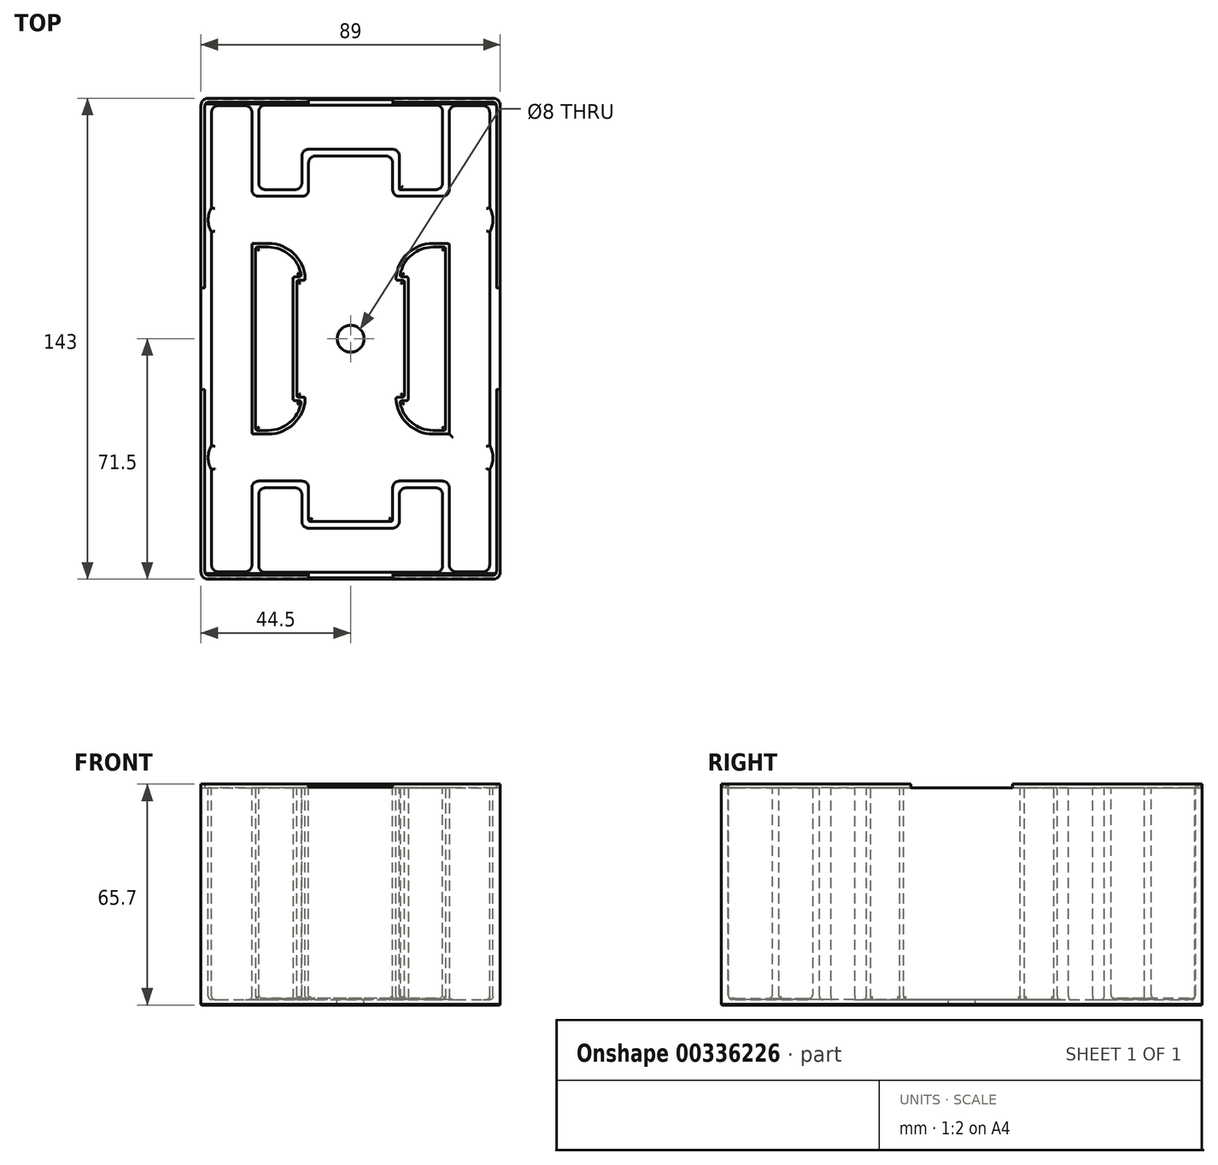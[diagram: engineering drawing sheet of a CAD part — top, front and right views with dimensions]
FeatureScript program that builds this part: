
annotation { "Feature Type Name" : "Feature", "Feature Type Description" : "" }
export const myFeature = defineFeature(function(context is Context, id is Id, definition is map)
    precondition{}
    {
        {
            var Q0;
            Q0=qCreatedBy(makeId("Top.planeOp"),FACE);
            var sketch = newSketch(context, id + "F0", { "sketchPlane" : qUnion([Q0])});
            skLineSegment(sketch, "E0.bottom", {"start": v(35.36, 35.36) * mm, "end": v(-35.36, 35.36) * mm, "construction": true});
            skLineSegment(sketch, "E0.top", {"start": v(35.36, -35.36) * mm, "end": v(-35.36, -35.36) * mm, "construction": true});
            skLineSegment(sketch, "E0.left", {"start": v(35.36, 35.36) * mm, "end": v(35.36, -35.36) * mm, "construction": true});
            skLineSegment(sketch, "E0.right", {"start": v(-35.36, 35.36) * mm, "end": v(-35.36, -35.36) * mm, "construction": true});
            skPoint(sketch, "E0.middle", {"position": v(0, 0) * mm});
            skLineSegment(sketch, "E1", {"start": v(35.36, 35.36) * mm, "end": v(-35.36, -35.36) * mm, "construction": true});
            skCircle(sketch, "E2", {"center": v(-35.36, 35.36) * mm, "radius": 34 * mm, "construction": true});
            skCircle(sketch, "E3.1.0", {"center": v(-35.36, -35.36) * mm, "radius": 34 * mm, "construction": true});
            skCircle(sketch, "E3.2.0", {"center": v(35.36, -35.36) * mm, "radius": 34 * mm, "construction": true});
            skCircle(sketch, "E3.3.0", {"center": v(35.36, 35.36) * mm, "radius": 34 * mm, "construction": true});
            skSolve(sketch);
        }
        {
            var Q0;
            Q0=qCreatedBy(makeId("Top.planeOp"),FACE);
            var sketch = newSketch(context, id + "F1", { "sketchPlane" : qUnion([Q0])});
            skLineSegment(sketch, "E4.0", {"start": v(35.36, 35.36) * mm, "end": v(-35.36, 35.36) * mm, "construction": true});
            skLineSegment(sketch, "E5.0", {"start": v(-35.36, 35.36) * mm, "end": v(-35.36, -35.36) * mm, "construction": true});
            skLineSegment(sketch, "E6.0", {"start": v(35.36, -35.36) * mm, "end": v(-35.36, -35.36) * mm, "construction": true});
            skLineSegment(sketch, "E7.0", {"start": v(35.36, 35.36) * mm, "end": v(35.36, -35.36) * mm, "construction": true});
            skArc(sketch, "E8", {"start": v(-35.36, 29.36) * mm, "mid": v(-41.36, 35.36) * mm, "end": v(-35.36, 41.36) * mm, "construction": true});
            skLineSegment(sketch, "E9", {"start": v(-35.36, 41.36) * mm, "end": v(0, 41.36) * mm, "construction": true});
            skLineSegment(sketch, "E10", {"start": v(-12.5, 0) * mm, "end": v(-12.5, 17.36) * mm, "construction": true});
            skLineSegment(sketch, "E11", {"start": v(-35.36, 29.36) * mm, "end": v(-24.5, 29.36) * mm, "construction": true});
            skPoint(sketch, "E12.visualSharp", {"position": v(-12.5, 29.36) * mm});
            skArc(sketch, "E12.filletArc", {"start": v(-12.5, 17.36) * mm, "mid": v(-16.01, 25.84) * mm, "end": v(-24.5, 29.36) * mm, "construction": true});
            skArc(sketch, "E13.MirrorCS", {"start": v(35.36, 29.36) * mm, "mid": v(41.36, 35.36) * mm, "end": v(35.36, 41.36) * mm, "construction": true});
            skLineSegment(sketch, "E14.MirrorCS", {"start": v(35.36, 41.36) * mm, "end": v(0, 41.36) * mm, "construction": true});
            skLineSegment(sketch, "E15.MirrorCS", {"start": v(35.36, 29.36) * mm, "end": v(24.5, 29.36) * mm, "construction": true});
            skArc(sketch, "E16.MirrorCS", {"start": v(12.5, 17.36) * mm, "mid": v(16.01, 25.84) * mm, "end": v(24.5, 29.36) * mm, "construction": true});
            skLineSegment(sketch, "E17.MirrorCS", {"start": v(12.5, 0) * mm, "end": v(12.5, 17.36) * mm, "construction": true});
            skArc(sketch, "E18.MirrorCS", {"start": v(-35.36, -29.36) * mm, "mid": v(-41.36, -35.36) * mm, "end": v(-35.36, -41.36) * mm, "construction": true});
            skArc(sketch, "E19.MirrorCS", {"start": v(35.36, -29.36) * mm, "mid": v(41.36, -35.36) * mm, "end": v(35.36, -41.36) * mm, "construction": true});
            skLineSegment(sketch, "E20.MirrorCS", {"start": v(35.36, -41.36) * mm, "end": v(0, -41.36) * mm, "construction": true});
            skLineSegment(sketch, "E21.MirrorCS", {"start": v(-35.36, -29.36) * mm, "end": v(-24.5, -29.36) * mm, "construction": true});
            skArc(sketch, "E22.MirrorCS", {"start": v(-12.5, -17.36) * mm, "mid": v(-16.01, -25.84) * mm, "end": v(-24.5, -29.36) * mm, "construction": true});
            skArc(sketch, "E23.MirrorCS", {"start": v(12.5, -17.36) * mm, "mid": v(16.01, -25.84) * mm, "end": v(24.5, -29.36) * mm, "construction": true});
            skLineSegment(sketch, "E24.MirrorCS", {"start": v(35.36, -29.36) * mm, "end": v(24.5, -29.36) * mm, "construction": true});
            skLineSegment(sketch, "E25.MirrorCS", {"start": v(-12.5, 0) * mm, "end": v(-12.5, -17.36) * mm, "construction": true});
            skLineSegment(sketch, "E26.MirrorCS", {"start": v(12.5, 0) * mm, "end": v(12.5, -17.36) * mm, "construction": true});
            skLineSegment(sketch, "E27.MirrorCS", {"start": v(-35.36, -41.36) * mm, "end": v(0, -41.36) * mm, "construction": true});
            skArc(sketch, "E28.0", {"start": v(-35.36, 28.36) * mm, "mid": v(-42.36, 35.36) * mm, "end": v(-35.36, 42.36) * mm});
            skLineSegment(sketch, "E28.1", {"start": v(-35.36, 28.36) * mm, "end": v(-24.5, 28.36) * mm});
            skArc(sketch, "E28.2", {"start": v(-13.5, 17.36) * mm, "mid": v(-16.72, 25.13) * mm, "end": v(-24.5, 28.36) * mm});
            skLineSegment(sketch, "E28.3", {"start": v(-13.5, 0) * mm, "end": v(-13.5, 17.36) * mm, "construction": true});
            skLineSegment(sketch, "E28.4", {"start": v(-13.5, 0) * mm, "end": v(-13.5, -17.36) * mm, "construction": true});
            skLineSegment(sketch, "E28.5", {"start": v(-35.36, 42.36) * mm, "end": v(0, 42.36) * mm});
            skArc(sketch, "E28.6", {"start": v(-13.5, -17.36) * mm, "mid": v(-16.72, -25.13) * mm, "end": v(-24.5, -28.36) * mm});
            skLineSegment(sketch, "E28.7", {"start": v(-35.36, -28.36) * mm, "end": v(-24.5, -28.36) * mm});
            skArc(sketch, "E28.8", {"start": v(-35.36, -28.36) * mm, "mid": v(-42.36, -35.36) * mm, "end": v(-35.36, -42.36) * mm});
            skLineSegment(sketch, "E28.9", {"start": v(-35.36, -42.36) * mm, "end": v(0, -42.36) * mm});
            skArc(sketch, "E28.10", {"start": v(13.5, 17.36) * mm, "mid": v(16.72, 25.13) * mm, "end": v(24.5, 28.36) * mm});
            skLineSegment(sketch, "E28.11", {"start": v(35.36, 28.36) * mm, "end": v(24.5, 28.36) * mm});
            skArc(sketch, "E28.12", {"start": v(35.36, 28.36) * mm, "mid": v(42.36, 35.36) * mm, "end": v(35.36, 42.36) * mm});
            skLineSegment(sketch, "E28.13", {"start": v(35.36, 42.36) * mm, "end": v(0, 42.36) * mm});
            skLineSegment(sketch, "E28.14", {"start": v(13.5, 0) * mm, "end": v(13.5, 17.36) * mm, "construction": true});
            skLineSegment(sketch, "E28.15", {"start": v(13.5, 0) * mm, "end": v(13.5, -17.36) * mm, "construction": true});
            skArc(sketch, "E28.16", {"start": v(13.5, -17.36) * mm, "mid": v(16.72, -25.13) * mm, "end": v(24.5, -28.36) * mm});
            skLineSegment(sketch, "E28.17", {"start": v(35.36, -28.36) * mm, "end": v(24.5, -28.36) * mm});
            skArc(sketch, "E28.18", {"start": v(35.36, -28.36) * mm, "mid": v(42.36, -35.36) * mm, "end": v(35.36, -42.36) * mm});
            skLineSegment(sketch, "E28.19", {"start": v(35.36, -42.36) * mm, "end": v(0, -42.36) * mm});
            skLineSegment(sketch, "E29", {"start": v(-13.5, 0) * mm, "end": v(-16, 0) * mm});
            skLineSegment(sketch, "E30", {"start": v(-16, 0) * mm, "end": v(-16, -17.36) * mm});
            skLineSegment(sketch, "E31", {"start": v(-16, -17.36) * mm, "end": v(-13.5, -17.36) * mm});
            skLineSegment(sketch, "E32.MirrorCS", {"start": v(13.5, 0) * mm, "end": v(16, 0) * mm});
            skLineSegment(sketch, "E33.MirrorCS", {"start": v(16, 0) * mm, "end": v(16, -17.36) * mm});
            skLineSegment(sketch, "E34.MirrorCS", {"start": v(16, -17.36) * mm, "end": v(13.5, -17.36) * mm});
            skLineSegment(sketch, "E35", {"start": v(-12.5, 42.36) * mm, "end": v(-12.5, 54.36) * mm});
            skLineSegment(sketch, "E36", {"start": v(-12.5, 54.36) * mm, "end": v(12.5, 54.36) * mm});
            skLineSegment(sketch, "E37", {"start": v(12.5, 54.36) * mm, "end": v(12.5, 42.36) * mm});
            skLineSegment(sketch, "E38", {"start": v(-13.5, 17.36) * mm, "end": v(-16, 17.36) * mm});
            skLineSegment(sketch, "E39", {"start": v(-16, 17.36) * mm, "end": v(-16, 0) * mm});
            skLineSegment(sketch, "E40", {"start": v(13.5, 17.36) * mm, "end": v(16, 17.36) * mm});
            skLineSegment(sketch, "E41", {"start": v(16, 17.36) * mm, "end": v(16, 0) * mm});
            skLineSegment(sketch, "E42.MirrorCS", {"start": v(-12.5, -42.36) * mm, "end": v(-12.5, -54.36) * mm});
            skLineSegment(sketch, "E43.MirrorCS", {"start": v(-12.5, -54.36) * mm, "end": v(12.5, -54.36) * mm});
            skLineSegment(sketch, "E44.MirrorCS", {"start": v(12.5, -54.36) * mm, "end": v(12.5, -42.36) * mm});
            skSolve(sketch);
        }
        {
            var Q0;
            Q0=qCreatedBy(makeId("Top.planeOp"),FACE);
            var sketch = newSketch(context, id + "F2", { "sketchPlane" : qUnion([Q0])});
            skCircle(sketch, "E45.0", {"center": v(-35.36, 35.36) * mm, "radius": 34 * mm, "construction": true});
            skCircle(sketch, "E46.0", {"center": v(35.36, 35.36) * mm, "radius": 34 * mm, "construction": true});
            skCircle(sketch, "E47.0", {"center": v(-35.36, -35.36) * mm, "radius": 34 * mm, "construction": true});
            skCircle(sketch, "E48.0", {"center": v(35.36, -35.36) * mm, "radius": 34 * mm, "construction": true});
            skLineSegment(sketch, "E49.0", {"start": v(35.36, -35.36) * mm, "end": v(-35.36, -35.36) * mm, "construction": true});
            skLineSegment(sketch, "E50.0", {"start": v(-35.36, 35.36) * mm, "end": v(-35.36, -35.36) * mm, "construction": true});
            skLineSegment(sketch, "E51.0", {"start": v(35.36, 35.36) * mm, "end": v(-35.36, 35.36) * mm, "construction": true});
            skLineSegment(sketch, "E52.0", {"start": v(35.36, 35.36) * mm, "end": v(35.36, -35.36) * mm, "construction": true});
            skLineSegment(sketch, "E53.bottom", {"start": v(-29.36, 69.36) * mm, "end": v(-41.36, 69.36) * mm});
            skLineSegment(sketch, "E53.top", {"start": v(-29.36, -69.36) * mm, "end": v(-41.36, -69.36) * mm});
            skLineSegment(sketch, "E53.left", {"start": v(-29.36, 69.36) * mm, "end": v(-29.36, -69.36) * mm});
            skLineSegment(sketch, "E53.right", {"start": v(-41.36, 69.36) * mm, "end": v(-41.36, -69.36) * mm});
            skPoint(sketch, "E53.middle", {"position": v(-35.36, 0) * mm});
            skLineSegment(sketch, "E54.bottom", {"start": v(41.36, 69.36) * mm, "end": v(29.36, 69.36) * mm});
            skLineSegment(sketch, "E54.top", {"start": v(41.36, -69.36) * mm, "end": v(29.36, -69.36) * mm});
            skLineSegment(sketch, "E54.left", {"start": v(41.36, 69.36) * mm, "end": v(41.36, -69.36) * mm});
            skLineSegment(sketch, "E54.right", {"start": v(29.36, 69.36) * mm, "end": v(29.36, -69.36) * mm});
            skPoint(sketch, "E54.middle", {"position": v(35.36, 0) * mm});
            skSolve(sketch);
        }
        {
            var Q0;
            Q0=qCreatedBy(makeId("Front.planeOp"),FACE);
            var sketch = newSketch(context, id + "F3", { "sketchPlane" : qUnion([Q0])});
            skLineSegment(sketch, "E55", {"start": v(0, 0) * mm, "end": v(0, -3) * mm});
            skLineSegment(sketch, "E56", {"start": v(0, -3) * mm, "end": v(0, -4.6) * mm});
            skLineSegment(sketch, "E57", {"start": v(0, 0) * mm, "end": v(0, 60) * mm});
            skLineSegment(sketch, "E58", {"start": v(0, 60) * mm, "end": v(0, 61.1) * mm});
            skSolve(sketch);
        }
        {
            var Q0;
            Q0=qCreatedBy(makeId("Top.planeOp"),FACE);
            var sketch = newSketch(context, id + "F4", { "sketchPlane" : qUnion([Q0])});
            skLineSegment(sketch, "E59.0.0", {"start": v(-41.36, -69.36) * mm, "end": v(-29.36, -69.36) * mm, "construction": true});
            skLineSegment(sketch, "E59.0.1", {"start": v(-29.36, -69.36) * mm, "end": v(-29.36, 69.36) * mm, "construction": true});
            skLineSegment(sketch, "E59.0.2", {"start": v(-29.36, 69.36) * mm, "end": v(-41.36, 69.36) * mm, "construction": true});
            skLineSegment(sketch, "E59.0.3", {"start": v(-41.36, 69.36) * mm, "end": v(-41.36, -69.36) * mm, "construction": true});
            skLineSegment(sketch, "E60.0.0", {"start": v(29.36, -69.36) * mm, "end": v(41.36, -69.36) * mm, "construction": true});
            skLineSegment(sketch, "E60.0.1", {"start": v(41.36, -69.36) * mm, "end": v(41.36, 69.36) * mm, "construction": true});
            skLineSegment(sketch, "E60.0.2", {"start": v(41.36, 69.36) * mm, "end": v(29.36, 69.36) * mm, "construction": true});
            skLineSegment(sketch, "E60.0.3", {"start": v(29.36, 69.36) * mm, "end": v(29.36, -69.36) * mm, "construction": true});
            skLineSegment(sketch, "E61.bottom", {"start": v(-44.5, 71.5) * mm, "end": v(44.5, 71.5) * mm});
            skLineSegment(sketch, "E61.top", {"start": v(-44.5, -71.5) * mm, "end": v(44.5, -71.5) * mm});
            skLineSegment(sketch, "E61.left", {"start": v(-44.5, 71.5) * mm, "end": v(-44.5, -71.5) * mm});
            skLineSegment(sketch, "E61.right", {"start": v(44.5, 71.5) * mm, "end": v(44.5, -71.5) * mm});
            skPoint(sketch, "E61.middle", {"position": v(0, 0) * mm});
            skPoint(sketch, "E62.0", {"position": v(42.36, -35.36) * mm});
            skSolve(sketch);
        }
        {
            var Q0;
            Q0 = qSketchRegion(id + "F4", true);
            var Q1;
            Q1=sQuery(id+"F3.wireOp",EDGE,"E57");
            var Q2;
            Q2=sQuery(id+"F3.wireOp",EDGE,"E58");
            sweep(context, id + "F5", {"profiles" : qUnion([Q0]), "path" : qUnion([Q1, Q2])});
        }
        {
            var Q0;
            Q0 = qSketchRegion(id + "F4", true);
            var Q1;
            Q1=sQuery(id+"F3.wireOp",EDGE,"E55");
            var Q2;
            Q2=sQuery(id+"F3.wireOp",EDGE,"E56");
            sweep(context, id + "F6", {"operationType" : NewBodyOperationType.ADD, "profiles" : qUnion([Q0]), "path" : qUnion([Q1, Q2])});
        }
        {
            var Q0;
            Q0 = qSketchRegion(id + "F1", true);
            var Q1;
            Q1=sQuery(id+"F3.wireOp",EDGE,"E57");
            var Q2;
            Q2=sQuery(id+"F3.wireOp",EDGE,"E58");
            sweep(context, id + "F7", {"operationType" : NewBodyOperationType.REMOVE, "profiles" : qUnion([Q0]), "path" : qUnion([Q1, Q2])});
        }
        {
            var Q0;
            Q0 = qSketchRegion(id + "F1", true);
            var Q1;
            Q1=sQuery(id+"F3.wireOp",EDGE,"E55");
            sweep(context, id + "F8", {"operationType" : NewBodyOperationType.REMOVE, "profiles" : qUnion([Q0]), "path" : qUnion([Q1])});
        }
        {
            var Q0;
            Q0 = qSketchRegion(id + "F2", true);
            var Q1;
            Q1=sQuery(id+"F3.wireOp",EDGE,"E57");
            var Q2;
            Q2=sQuery(id+"F3.wireOp",EDGE,"E58");
            sweep(context, id + "F9", {"operationType" : NewBodyOperationType.REMOVE, "profiles" : qUnion([Q0]), "path" : qUnion([Q1, Q2])});
        }
        {
            var Q0;
            Q0 = qSketchRegion(id + "F2", true);
            var Q1;
            Q1=sQuery(id+"F3.wireOp",EDGE,"E55");
            sweep(context, id + "F10", {"operationType" : NewBodyOperationType.REMOVE, "profiles" : qUnion([Q0]), "path" : qUnion([Q1])});
        }
        {
            var Q0;
            {var subQ5=sQuery(id+"F3.wireOp",EDGE,"E57");var subQ10=sQuery(id+"F4.wireOp",EDGE,"E61.right");var subQ11=sQuery(id+"F4.wireOp",EDGE,"E61.left");var subQ13=sQuery(id+"F4.wireOp",EDGE,"E61.top");var subQ15=sQuery(id+"F4.wireOp",EDGE,"E61.bottom");Q0=makeQuery(id+"F9.boolean.opBoolean","SPLIT",FACE,{"disambiguationData":[TD([makeQuery(id+"F5.opSweep","SWEPT_FACE",FACE,{"disambiguationData":[OSD([subQ5,subQ15])]})])],"derivedFrom":makeQuery(id+"F5.opSweep","CAP_FACE",FACE,{"disambiguationData":[OSD([sQuery(id+"F3.wireOp",VERTEX,"E58.end"),subQ15,subQ13,subQ11,subQ10])],"isStart":false})});}
            shell(context, id + "F11", {"entities" : qUnion([Q0]), "thickness" : 2 * mm});
        }
        {
            var Q0;
            {var subQ0=sQuery(id+"F3.wireOp",EDGE,"E57");var subQ5=sQuery(id+"F1.wireOp",EDGE,"E28.1");Q0=makeQuery(id+"F9.boolean.opBoolean","SPLIT",FACE,{"disambiguationData":[TD([makeQuery(id+"F7.boolean.opBoolean","COPY",FACE,{"derivedFrom":makeQuery(id+"F7.opSweep","SWEPT_FACE",FACE,{"disambiguationData":[OSD([subQ5,subQ0])]})})])],"derivedFrom":makeQuery(id+"F5.opSweep","CAP_FACE",FACE,{"disambiguationData":[OSD([sQuery(id+"F3.wireOp",VERTEX,"E58.end"),sQuery(id+"F4.wireOp",EDGE,"E61.bottom"),sQuery(id+"F4.wireOp",EDGE,"E61.top"),sQuery(id+"F4.wireOp",EDGE,"E61.left"),sQuery(id+"F4.wireOp",EDGE,"E61.right")])],"isStart":false})});}
            var sketch = newSketch(context, id + "F12", { "sketchPlane" : qUnion([Q0])});
            skLineSegment(sketch, "E63.0", {"start": v(-24.5, -27.26) * mm, "end": v(-28.26, -27.26) * mm});
            skArc(sketch, "E63.1", {"start": v(-14.66, -18.46) * mm, "mid": v(-17.9, -24.73) * mm, "end": v(-24.5, -27.26) * mm});
            skLineSegment(sketch, "E63.2", {"start": v(-28.26, -27.26) * mm, "end": v(-28.26, 27.26) * mm});
            skLineSegment(sketch, "E63.3", {"start": v(-17.1, -18.46) * mm, "end": v(-14.66, -18.46) * mm});
            skLineSegment(sketch, "E63.4", {"start": v(-28.26, 27.26) * mm, "end": v(-24.5, 27.26) * mm});
            skArc(sketch, "E63.5", {"start": v(-24.5, 27.26) * mm, "mid": v(-17.9, 24.73) * mm, "end": v(-14.66, 18.46) * mm});
            skLineSegment(sketch, "E63.6", {"start": v(-14.66, 18.46) * mm, "end": v(-17.1, 18.46) * mm});
            skLineSegment(sketch, "E63.7", {"start": v(-17.1, 18.46) * mm, "end": v(-17.1, -18.46) * mm});
            skLineSegment(sketch, "E64.MirrorCS", {"start": v(28.26, -27.26) * mm, "end": v(28.26, 27.26) * mm});
            skLineSegment(sketch, "E65.MirrorCS", {"start": v(28.26, 27.26) * mm, "end": v(24.5, 27.26) * mm});
            skArc(sketch, "E66.MirrorCS", {"start": v(24.5, 27.26) * mm, "mid": v(17.9, 24.73) * mm, "end": v(14.66, 18.46) * mm});
            skLineSegment(sketch, "E67.MirrorCS", {"start": v(14.66, 18.46) * mm, "end": v(17.1, 18.46) * mm});
            skLineSegment(sketch, "E68.MirrorCS", {"start": v(17.1, 18.46) * mm, "end": v(17.1, -18.46) * mm});
            skLineSegment(sketch, "E69.MirrorCS", {"start": v(17.1, -18.46) * mm, "end": v(14.66, -18.46) * mm});
            skArc(sketch, "E70.MirrorCS", {"start": v(14.66, -18.46) * mm, "mid": v(17.9, -24.73) * mm, "end": v(24.5, -27.26) * mm});
            skLineSegment(sketch, "E71.MirrorCS", {"start": v(24.5, -27.26) * mm, "end": v(28.26, -27.26) * mm});
            skSolve(sketch);
        }
        {
            var Q0;
            Q0 = qSketchRegion(id + "F12", true);
            var Q1;
            Q1=sQuery(id+"F3.wireOp",EDGE,"E58");
            var Q2;
            Q2=sQuery(id+"F3.wireOp",EDGE,"E57");
            var Q3;
            Q3=sQuery(id+"F3.wireOp",EDGE,"E55");
            sweep(context, id + "F13", {"operationType" : NewBodyOperationType.REMOVE, "profiles" : qUnion([Q0]), "path" : qUnion([Q1, Q2, Q3])});
        }
        {
            var Q0;
            {var subQ0=sQuery(id+"F2.wireOp",EDGE,"E53.right");var subQ1=sQuery(id+"F2.wireOp",EDGE,"E53.bottom");Q0=makeQuery(id+"F10.boolean.opBoolean","MERGE",EDGE,{"derivedFrom":[makeQuery(id+"F9.boolean.opBoolean","COPY",EDGE,{"derivedFrom":makeQuery(id+"F9.opSweep","SWEPT_EDGE",EDGE,{"disambiguationData":[OSD([subQ1,subQ0,sQuery(id+"F3.wireOp",EDGE,"E57")])]})}),makeQuery(id+"F10.opSweep","SWEPT_EDGE",EDGE,{"disambiguationData":[OSD([subQ1,subQ0,sQuery(id+"F3.wireOp",EDGE,"E55")])]})]});}
            var Q1;
            {var subQ0=sQuery(id+"F2.wireOp",EDGE,"E54.left");var subQ1=sQuery(id+"F2.wireOp",EDGE,"E54.bottom");Q1=makeQuery(id+"F10.boolean.opBoolean","MERGE",EDGE,{"derivedFrom":[makeQuery(id+"F9.boolean.opBoolean","COPY",EDGE,{"derivedFrom":makeQuery(id+"F9.opSweep","SWEPT_EDGE",EDGE,{"disambiguationData":[OSD([subQ1,subQ0,sQuery(id+"F3.wireOp",EDGE,"E57")])]})}),makeQuery(id+"F10.opSweep","SWEPT_EDGE",EDGE,{"disambiguationData":[OSD([subQ1,subQ0,sQuery(id+"F3.wireOp",EDGE,"E55")])]})]});}
            var Q2;
            {var subQ0=sQuery(id+"F2.wireOp",EDGE,"E53.right");var subQ1=sQuery(id+"F2.wireOp",EDGE,"E53.top");Q2=makeQuery(id+"F10.boolean.opBoolean","MERGE",EDGE,{"derivedFrom":[makeQuery(id+"F9.boolean.opBoolean","COPY",EDGE,{"derivedFrom":makeQuery(id+"F9.opSweep","SWEPT_EDGE",EDGE,{"disambiguationData":[OSD([subQ1,subQ0,sQuery(id+"F3.wireOp",EDGE,"E57")])]})}),makeQuery(id+"F10.opSweep","SWEPT_EDGE",EDGE,{"disambiguationData":[OSD([subQ1,subQ0,sQuery(id+"F3.wireOp",EDGE,"E55")])]})]});}
            var Q3;
            {var subQ0=sQuery(id+"F2.wireOp",EDGE,"E54.left");var subQ1=sQuery(id+"F2.wireOp",EDGE,"E54.top");Q3=makeQuery(id+"F10.boolean.opBoolean","MERGE",EDGE,{"derivedFrom":[makeQuery(id+"F9.boolean.opBoolean","COPY",EDGE,{"derivedFrom":makeQuery(id+"F9.opSweep","SWEPT_EDGE",EDGE,{"disambiguationData":[OSD([subQ1,subQ0,sQuery(id+"F3.wireOp",EDGE,"E57")])]})}),makeQuery(id+"F10.opSweep","SWEPT_EDGE",EDGE,{"disambiguationData":[OSD([subQ1,subQ0,sQuery(id+"F3.wireOp",EDGE,"E55")])]})]});}
            var Q4;
            {var subQ0=sQuery(id+"F2.wireOp",EDGE,"E53.left");var subQ1=sQuery(id+"F2.wireOp",EDGE,"E53.bottom");Q4=makeQuery(id+"F10.boolean.opBoolean","MERGE",EDGE,{"derivedFrom":[makeQuery(id+"F9.boolean.opBoolean","COPY",EDGE,{"derivedFrom":makeQuery(id+"F9.opSweep","SWEPT_EDGE",EDGE,{"disambiguationData":[OSD([subQ1,subQ0,sQuery(id+"F3.wireOp",EDGE,"E57")])]})}),makeQuery(id+"F10.opSweep","SWEPT_EDGE",EDGE,{"disambiguationData":[OSD([subQ1,subQ0,sQuery(id+"F3.wireOp",EDGE,"E55")])]})]});}
            var Q5;
            {var subQ0=sQuery(id+"F2.wireOp",EDGE,"E54.right");var subQ1=sQuery(id+"F2.wireOp",EDGE,"E54.bottom");Q5=makeQuery(id+"F10.boolean.opBoolean","MERGE",EDGE,{"derivedFrom":[makeQuery(id+"F9.boolean.opBoolean","COPY",EDGE,{"derivedFrom":makeQuery(id+"F9.opSweep","SWEPT_EDGE",EDGE,{"disambiguationData":[OSD([subQ1,subQ0,sQuery(id+"F3.wireOp",EDGE,"E57")])]})}),makeQuery(id+"F10.opSweep","SWEPT_EDGE",EDGE,{"disambiguationData":[OSD([subQ1,subQ0,sQuery(id+"F3.wireOp",EDGE,"E55")])]})]});}
            var Q6;
            {var subQ0=sQuery(id+"F2.wireOp",EDGE,"E53.left");var subQ1=sQuery(id+"F2.wireOp",EDGE,"E53.top");Q6=makeQuery(id+"F10.boolean.opBoolean","MERGE",EDGE,{"derivedFrom":[makeQuery(id+"F9.boolean.opBoolean","COPY",EDGE,{"derivedFrom":makeQuery(id+"F9.opSweep","SWEPT_EDGE",EDGE,{"disambiguationData":[OSD([subQ1,subQ0,sQuery(id+"F3.wireOp",EDGE,"E57")])]})}),makeQuery(id+"F10.opSweep","SWEPT_EDGE",EDGE,{"disambiguationData":[OSD([subQ1,subQ0,sQuery(id+"F3.wireOp",EDGE,"E55")])]})]});}
            var Q7;
            {var subQ0=sQuery(id+"F2.wireOp",EDGE,"E54.right");var subQ1=sQuery(id+"F2.wireOp",EDGE,"E54.top");Q7=makeQuery(id+"F10.boolean.opBoolean","MERGE",EDGE,{"derivedFrom":[makeQuery(id+"F9.boolean.opBoolean","COPY",EDGE,{"derivedFrom":makeQuery(id+"F9.opSweep","SWEPT_EDGE",EDGE,{"disambiguationData":[OSD([subQ1,subQ0,sQuery(id+"F3.wireOp",EDGE,"E57")])]})}),makeQuery(id+"F10.opSweep","SWEPT_EDGE",EDGE,{"disambiguationData":[OSD([subQ1,subQ0,sQuery(id+"F3.wireOp",EDGE,"E55")])]})]});}
            var Q8;
            {var subQ0=sQuery(id+"F4.wireOp",EDGE,"E61.right");var subQ1=sQuery(id+"F4.wireOp",EDGE,"E61.top");Q8=makeQuery(id+"F6.boolean.opBoolean","MERGE",EDGE,{"derivedFrom":[makeQuery(id+"F5.opSweep","SWEPT_EDGE",EDGE,{"disambiguationData":[OSD([sQuery(id+"F3.wireOp",EDGE,"E57"),subQ1,subQ0])]}),makeQuery(id+"F6.opSweep","SWEPT_EDGE",EDGE,{"disambiguationData":[OSD([sQuery(id+"F3.wireOp",EDGE,"E55"),subQ1,subQ0])]})]});}
            var Q9;
            {var subQ0=sQuery(id+"F4.wireOp",EDGE,"E61.left");var subQ1=sQuery(id+"F4.wireOp",EDGE,"E61.top");Q9=makeQuery(id+"F6.boolean.opBoolean","MERGE",EDGE,{"derivedFrom":[makeQuery(id+"F5.opSweep","SWEPT_EDGE",EDGE,{"disambiguationData":[OSD([sQuery(id+"F3.wireOp",EDGE,"E57"),subQ1,subQ0])]}),makeQuery(id+"F6.opSweep","SWEPT_EDGE",EDGE,{"disambiguationData":[OSD([sQuery(id+"F3.wireOp",EDGE,"E55"),subQ1,subQ0])]})]});}
            var Q10;
            {var subQ0=sQuery(id+"F4.wireOp",EDGE,"E61.right");var subQ1=sQuery(id+"F4.wireOp",EDGE,"E61.bottom");Q10=makeQuery(id+"F6.boolean.opBoolean","MERGE",EDGE,{"derivedFrom":[makeQuery(id+"F5.opSweep","SWEPT_EDGE",EDGE,{"disambiguationData":[OSD([sQuery(id+"F3.wireOp",EDGE,"E57"),subQ1,subQ0])]}),makeQuery(id+"F6.opSweep","SWEPT_EDGE",EDGE,{"disambiguationData":[OSD([sQuery(id+"F3.wireOp",EDGE,"E55"),subQ1,subQ0])]})]});}
            var Q11;
            {var subQ0=sQuery(id+"F4.wireOp",EDGE,"E61.left");var subQ1=sQuery(id+"F4.wireOp",EDGE,"E61.bottom");Q11=makeQuery(id+"F6.boolean.opBoolean","MERGE",EDGE,{"derivedFrom":[makeQuery(id+"F5.opSweep","SWEPT_EDGE",EDGE,{"disambiguationData":[OSD([sQuery(id+"F3.wireOp",EDGE,"E57"),subQ1,subQ0])]}),makeQuery(id+"F6.opSweep","SWEPT_EDGE",EDGE,{"disambiguationData":[OSD([sQuery(id+"F3.wireOp",EDGE,"E55"),subQ1,subQ0])]})]});}
            var Q12;
            {var subQ0=sQuery(id+"F3.wireOp",EDGE,"E55");var subQ1=sQuery(id+"F1.wireOp",EDGE,"E28.5");Q12=makeQuery(id+"F10.boolean.opBoolean","INTERSECT",EDGE,{"derivedFrom":[makeQuery(id+"F8.boolean.opBoolean","MERGE",FACE,{"derivedFrom":[makeQuery(id+"F7.boolean.opBoolean","COPY",FACE,{"derivedFrom":makeQuery(id+"F7.opSweep","SWEPT_FACE",FACE,{"disambiguationData":[OSD([subQ1,sQuery(id+"F3.wireOp",EDGE,"E57")])]})}),makeQuery(id+"F8.opSweep","SWEPT_FACE",FACE,{"disambiguationData":[OSD([subQ1,subQ0])]})]}),makeQuery(id+"F10.opSweep","SWEPT_FACE",FACE,{"disambiguationData":[OSD([sQuery(id+"F2.wireOp",EDGE,"E53.left"),subQ0])]})]});}
            var Q13;
            {var subQ0=sQuery(id+"F1.wireOp",EDGE,"E35");var subQ1=sQuery(id+"F1.wireOp",EDGE,"E28.5");Q13=makeQuery(id+"F8.boolean.opBoolean","MERGE",EDGE,{"derivedFrom":[makeQuery(id+"F7.boolean.opBoolean","COPY",EDGE,{"derivedFrom":makeQuery(id+"F7.opSweep","SWEPT_EDGE",EDGE,{"disambiguationData":[OSD([subQ1,subQ0,sQuery(id+"F3.wireOp",EDGE,"E57")])]})}),makeQuery(id+"F8.opSweep","SWEPT_EDGE",EDGE,{"disambiguationData":[OSD([subQ1,subQ0,sQuery(id+"F3.wireOp",EDGE,"E55")])]})]});}
            var Q14;
            {var subQ0=sQuery(id+"F1.wireOp",EDGE,"E37");var subQ1=sQuery(id+"F1.wireOp",EDGE,"E28.13");Q14=makeQuery(id+"F8.boolean.opBoolean","MERGE",EDGE,{"derivedFrom":[makeQuery(id+"F7.boolean.opBoolean","COPY",EDGE,{"derivedFrom":makeQuery(id+"F7.opSweep","SWEPT_EDGE",EDGE,{"disambiguationData":[OSD([subQ1,subQ0,sQuery(id+"F3.wireOp",EDGE,"E57")])]})}),makeQuery(id+"F8.opSweep","SWEPT_EDGE",EDGE,{"disambiguationData":[OSD([subQ1,subQ0,sQuery(id+"F3.wireOp",EDGE,"E55")])]})]});}
            var Q15;
            {var subQ0=sQuery(id+"F3.wireOp",EDGE,"E55");var subQ1=sQuery(id+"F1.wireOp",EDGE,"E28.13");Q15=makeQuery(id+"F10.boolean.opBoolean","INTERSECT",EDGE,{"derivedFrom":[makeQuery(id+"F8.boolean.opBoolean","MERGE",FACE,{"derivedFrom":[makeQuery(id+"F7.boolean.opBoolean","COPY",FACE,{"derivedFrom":makeQuery(id+"F7.opSweep","SWEPT_FACE",FACE,{"disambiguationData":[OSD([subQ1,sQuery(id+"F3.wireOp",EDGE,"E57")])]})}),makeQuery(id+"F8.opSweep","SWEPT_FACE",FACE,{"disambiguationData":[OSD([subQ1,subQ0])]})]}),makeQuery(id+"F10.opSweep","SWEPT_FACE",FACE,{"disambiguationData":[OSD([sQuery(id+"F2.wireOp",EDGE,"E54.right"),subQ0])]})]});}
            var Q16;
            {var subQ0=sQuery(id+"F1.wireOp",EDGE,"E36");var subQ1=sQuery(id+"F1.wireOp",EDGE,"E35");Q16=makeQuery(id+"F8.boolean.opBoolean","MERGE",EDGE,{"derivedFrom":[makeQuery(id+"F7.boolean.opBoolean","COPY",EDGE,{"derivedFrom":makeQuery(id+"F7.opSweep","SWEPT_EDGE",EDGE,{"disambiguationData":[OSD([subQ1,subQ0,sQuery(id+"F3.wireOp",EDGE,"E57")])]})}),makeQuery(id+"F8.opSweep","SWEPT_EDGE",EDGE,{"disambiguationData":[OSD([subQ1,subQ0,sQuery(id+"F3.wireOp",EDGE,"E55")])]})]});}
            var Q17;
            {var subQ0=sQuery(id+"F1.wireOp",EDGE,"E37");var subQ1=sQuery(id+"F1.wireOp",EDGE,"E36");Q17=makeQuery(id+"F8.boolean.opBoolean","MERGE",EDGE,{"derivedFrom":[makeQuery(id+"F7.boolean.opBoolean","COPY",EDGE,{"derivedFrom":makeQuery(id+"F7.opSweep","SWEPT_EDGE",EDGE,{"disambiguationData":[OSD([subQ1,subQ0,sQuery(id+"F3.wireOp",EDGE,"E57")])]})}),makeQuery(id+"F8.opSweep","SWEPT_EDGE",EDGE,{"disambiguationData":[OSD([subQ1,subQ0,sQuery(id+"F3.wireOp",EDGE,"E55")])]})]});}
            var Q18;
            Q18=makeQuery(id+"F11.opShell","OFFSET_EDGE",EDGE,{"disambiguationData":[OSD([sQuery(id+"F1.wireOp",EDGE,"E28.5"),sQuery(id+"F1.wireOp",EDGE,"E35"),sQuery(id+"F3.wireOp",EDGE,"E55"),sQuery(id+"F3.wireOp",EDGE,"E57")])]});
            var Q19;
            Q19=makeQuery(id+"F11.opShell","OFFSET_EDGE",EDGE,{"disambiguationData":[OSD([sQuery(id+"F1.wireOp",EDGE,"E28.5"),sQuery(id+"F2.wireOp",EDGE,"E53.left"),sQuery(id+"F3.wireOp",EDGE,"E55"),sQuery(id+"F3.wireOp",EDGE,"E57")])]});
            var Q20;
            Q20=makeQuery(id+"F11.opShell","OFFSET_EDGE",EDGE,{"disambiguationData":[OSD([sQuery(id+"F1.wireOp",EDGE,"E36"),sQuery(id+"F1.wireOp",EDGE,"E37"),sQuery(id+"F3.wireOp",EDGE,"E55"),sQuery(id+"F3.wireOp",EDGE,"E57")])]});
            var Q21;
            Q21=makeQuery(id+"F11.opShell","OFFSET_EDGE",EDGE,{"disambiguationData":[OSD([sQuery(id+"F1.wireOp",EDGE,"E35"),sQuery(id+"F1.wireOp",EDGE,"E36"),sQuery(id+"F3.wireOp",EDGE,"E55"),sQuery(id+"F3.wireOp",EDGE,"E57")])]});
            var Q22;
            {var subQ0=sQuery(id+"F3.wireOp",EDGE,"E55");var subQ1=sQuery(id+"F2.wireOp",EDGE,"E54.right");var subQ3=sQuery(id+"F1.wireOp",EDGE,"E28.13");var subQ4=sQuery(id+"F4.wireOp",EDGE,"E61.bottom");var subQ5=sQuery(id+"F3.wireOp",EDGE,"E57");Q22=makeQuery(id+"F11.opShell","TWEAK_EDGE",EDGE,{"derivedFrom":[makeQuery(id+"F6.boolean.opBoolean","MERGE",FACE,{"derivedFrom":[makeQuery(id+"F5.opSweep","SWEPT_FACE",FACE,{"disambiguationData":[OSD([subQ5,subQ4])]}),makeQuery(id+"F6.opSweep","SWEPT_FACE",FACE,{"disambiguationData":[OSD([subQ0,subQ4])]})]}),makeQuery(id+"F10.boolean.opBoolean","MERGE",FACE,{"derivedFrom":[makeQuery(id+"F9.boolean.opBoolean","COPY",FACE,{"disambiguationData":[TD([makeQuery(id+"F7.boolean.opBoolean","COPY",FACE,{"derivedFrom":makeQuery(id+"F7.opSweep","SWEPT_FACE",FACE,{"disambiguationData":[OSD([subQ3,subQ5])]})})])],"derivedFrom":makeQuery(id+"F9.opSweep","SWEPT_FACE",FACE,{"disambiguationData":[OSD([subQ1,subQ5])]})}),makeQuery(id+"F10.opSweep","SWEPT_FACE",FACE,{"disambiguationData":[OSD([subQ1,subQ0])]})]})]});}
            var Q23;
            Q23=makeQuery(id+"F11.opShell","OFFSET_EDGE",EDGE,{"disambiguationData":[OSD([sQuery(id+"F1.wireOp",EDGE,"E28.13"),sQuery(id+"F2.wireOp",EDGE,"E54.right"),sQuery(id+"F3.wireOp",EDGE,"E55"),sQuery(id+"F3.wireOp",EDGE,"E57")])]});
            var Q24;
            {var subQ0=sQuery(id+"F3.wireOp",EDGE,"E55");var subQ1=sQuery(id+"F2.wireOp",EDGE,"E53.left");var subQ2=sQuery(id+"F2.wireOp",EDGE,"E53.top");var subQ5=sQuery(id+"F3.wireOp",EDGE,"E57");var subQ6=sQuery(id+"F4.wireOp",EDGE,"E61.top");Q24=makeQuery(id+"F11.opShell","TWEAK_EDGE",EDGE,{"derivedFrom":[makeQuery(id+"F6.boolean.opBoolean","MERGE",FACE,{"derivedFrom":[makeQuery(id+"F5.opSweep","SWEPT_FACE",FACE,{"disambiguationData":[OSD([subQ5,subQ6])]}),makeQuery(id+"F6.opSweep","SWEPT_FACE",FACE,{"disambiguationData":[OSD([subQ0,subQ6])]})]}),makeQuery(id+"F10.boolean.opBoolean","MERGE",FACE,{"derivedFrom":[makeQuery(id+"F9.boolean.opBoolean","COPY",FACE,{"disambiguationData":[TD([makeQuery(id+"F9.opSweep","SWEPT_FACE",FACE,{"disambiguationData":[OSD([subQ2,subQ5])]})])],"derivedFrom":makeQuery(id+"F9.opSweep","SWEPT_FACE",FACE,{"disambiguationData":[OSD([subQ1,subQ5])]})}),makeQuery(id+"F10.opSweep","SWEPT_FACE",FACE,{"disambiguationData":[OSD([subQ1,subQ0])]})]})]});}
            var Q25;
            {var subQ0=sQuery(id+"F3.wireOp",EDGE,"E55");var subQ1=sQuery(id+"F2.wireOp",EDGE,"E54.right");var subQ4=sQuery(id+"F2.wireOp",EDGE,"E54.top");var subQ5=sQuery(id+"F4.wireOp",EDGE,"E61.top");var subQ6=sQuery(id+"F3.wireOp",EDGE,"E57");Q25=makeQuery(id+"F11.opShell","TWEAK_EDGE",EDGE,{"derivedFrom":[makeQuery(id+"F6.boolean.opBoolean","MERGE",FACE,{"derivedFrom":[makeQuery(id+"F5.opSweep","SWEPT_FACE",FACE,{"disambiguationData":[OSD([subQ6,subQ5])]}),makeQuery(id+"F6.opSweep","SWEPT_FACE",FACE,{"disambiguationData":[OSD([subQ0,subQ5])]})]}),makeQuery(id+"F10.boolean.opBoolean","MERGE",FACE,{"derivedFrom":[makeQuery(id+"F9.boolean.opBoolean","COPY",FACE,{"disambiguationData":[TD([makeQuery(id+"F9.opSweep","SWEPT_FACE",FACE,{"disambiguationData":[OSD([subQ4,subQ6])]})])],"derivedFrom":makeQuery(id+"F9.opSweep","SWEPT_FACE",FACE,{"disambiguationData":[OSD([subQ1,subQ6])]})}),makeQuery(id+"F10.opSweep","SWEPT_FACE",FACE,{"disambiguationData":[OSD([subQ1,subQ0])]})]})]});}
            var Q26;
            {var subQ0=sQuery(id+"F3.wireOp",EDGE,"E55");var subQ1=sQuery(id+"F1.wireOp",EDGE,"E28.19");var subQ2=sQuery(id+"F1.wireOp",EDGE,"E28.9");Q26=makeQuery(id+"F10.boolean.opBoolean","INTERSECT",EDGE,{"derivedFrom":[makeQuery(id+"F8.boolean.opBoolean","MERGE",FACE,{"derivedFrom":[makeQuery(id+"F7.boolean.opBoolean","COPY",FACE,{"derivedFrom":makeQuery(id+"F7.opSweep","SWEPT_FACE",FACE,{"disambiguationData":[OSD([subQ2,subQ1,sQuery(id+"F3.wireOp",EDGE,"E57")])]})}),makeQuery(id+"F8.opSweep","SWEPT_FACE",FACE,{"disambiguationData":[OSD([subQ2,subQ1,subQ0])]})]}),makeQuery(id+"F10.opSweep","SWEPT_FACE",FACE,{"disambiguationData":[OSD([sQuery(id+"F2.wireOp",EDGE,"E53.left"),subQ0])]})]});}
            var Q27;
            {var subQ0=sQuery(id+"F3.wireOp",EDGE,"E55");var subQ1=sQuery(id+"F1.wireOp",EDGE,"E28.19");var subQ2=sQuery(id+"F1.wireOp",EDGE,"E28.9");Q27=makeQuery(id+"F10.boolean.opBoolean","INTERSECT",EDGE,{"derivedFrom":[makeQuery(id+"F8.boolean.opBoolean","MERGE",FACE,{"derivedFrom":[makeQuery(id+"F7.boolean.opBoolean","COPY",FACE,{"derivedFrom":makeQuery(id+"F7.opSweep","SWEPT_FACE",FACE,{"disambiguationData":[OSD([subQ2,subQ1,sQuery(id+"F3.wireOp",EDGE,"E57")])]})}),makeQuery(id+"F8.opSweep","SWEPT_FACE",FACE,{"disambiguationData":[OSD([subQ2,subQ1,subQ0])]})]}),makeQuery(id+"F10.opSweep","SWEPT_FACE",FACE,{"disambiguationData":[OSD([sQuery(id+"F2.wireOp",EDGE,"E54.right"),subQ0])]})]});}
            var Q28;
            Q28=makeQuery(id+"F11.opShell","OFFSET_EDGE",EDGE,{"disambiguationData":[OSD([sQuery(id+"F1.wireOp",EDGE,"E28.9"),sQuery(id+"F1.wireOp",EDGE,"E28.19"),sQuery(id+"F2.wireOp",EDGE,"E53.left"),sQuery(id+"F3.wireOp",EDGE,"E55"),sQuery(id+"F3.wireOp",EDGE,"E57")])]});
            var Q29;
            Q29=makeQuery(id+"F11.opShell","OFFSET_EDGE",EDGE,{"disambiguationData":[OSD([sQuery(id+"F1.wireOp",EDGE,"E28.9"),sQuery(id+"F1.wireOp",EDGE,"E28.19"),sQuery(id+"F2.wireOp",EDGE,"E54.right"),sQuery(id+"F3.wireOp",EDGE,"E55"),sQuery(id+"F3.wireOp",EDGE,"E57")])]});
            var Q30;
            {var subQ0=sQuery(id+"F3.wireOp",EDGE,"E55");var subQ1=sQuery(id+"F2.wireOp",EDGE,"E53.left");var subQ3=sQuery(id+"F3.wireOp",EDGE,"E57");var subQ4=sQuery(id+"F1.wireOp",EDGE,"E28.5");var subQ5=sQuery(id+"F4.wireOp",EDGE,"E61.bottom");Q30=makeQuery(id+"F11.opShell","TWEAK_EDGE",EDGE,{"derivedFrom":[makeQuery(id+"F6.boolean.opBoolean","MERGE",FACE,{"derivedFrom":[makeQuery(id+"F5.opSweep","SWEPT_FACE",FACE,{"disambiguationData":[OSD([subQ3,subQ5])]}),makeQuery(id+"F6.opSweep","SWEPT_FACE",FACE,{"disambiguationData":[OSD([subQ0,subQ5])]})]}),makeQuery(id+"F10.boolean.opBoolean","MERGE",FACE,{"derivedFrom":[makeQuery(id+"F9.boolean.opBoolean","COPY",FACE,{"disambiguationData":[TD([makeQuery(id+"F7.boolean.opBoolean","COPY",FACE,{"derivedFrom":makeQuery(id+"F7.opSweep","SWEPT_FACE",FACE,{"disambiguationData":[OSD([subQ4,subQ3])]})})])],"derivedFrom":makeQuery(id+"F9.opSweep","SWEPT_FACE",FACE,{"disambiguationData":[OSD([subQ1,subQ3])]})}),makeQuery(id+"F10.opSweep","SWEPT_FACE",FACE,{"disambiguationData":[OSD([subQ1,subQ0])]})]})]});}
            var Q31;
            Q31=makeQuery(id+"F11.opShell","OFFSET_EDGE",EDGE,{"disambiguationData":[OSD([sQuery(id+"F1.wireOp",EDGE,"E42.MirrorCS"),sQuery(id+"F1.wireOp",EDGE,"E43.MirrorCS"),sQuery(id+"F3.wireOp",EDGE,"E55"),sQuery(id+"F3.wireOp",EDGE,"E57")])]});
            var Q32;
            Q32=makeQuery(id+"F11.opShell","OFFSET_EDGE",EDGE,{"disambiguationData":[OSD([sQuery(id+"F1.wireOp",EDGE,"E43.MirrorCS"),sQuery(id+"F1.wireOp",EDGE,"E44.MirrorCS"),sQuery(id+"F3.wireOp",EDGE,"E55"),sQuery(id+"F3.wireOp",EDGE,"E57")])]});
            var Q33;
            {var subQ0=sQuery(id+"F1.wireOp",EDGE,"E42.MirrorCS");var subQ1=sQuery(id+"F1.wireOp",EDGE,"E28.9");Q33=makeQuery(id+"F8.boolean.opBoolean","MERGE",EDGE,{"derivedFrom":[makeQuery(id+"F7.boolean.opBoolean","COPY",EDGE,{"derivedFrom":makeQuery(id+"F7.opSweep","SWEPT_EDGE",EDGE,{"disambiguationData":[OSD([subQ1,subQ0,sQuery(id+"F3.wireOp",EDGE,"E57")])]})}),makeQuery(id+"F8.opSweep","SWEPT_EDGE",EDGE,{"disambiguationData":[OSD([subQ1,subQ0,sQuery(id+"F3.wireOp",EDGE,"E55")])]})]});}
            var Q34;
            Q34=makeQuery(id+"F11.opShell","OFFSET_EDGE",EDGE,{"disambiguationData":[OSD([sQuery(id+"F1.wireOp",EDGE,"E28.19"),sQuery(id+"F1.wireOp",EDGE,"E44.MirrorCS"),sQuery(id+"F3.wireOp",EDGE,"E55"),sQuery(id+"F3.wireOp",EDGE,"E57")])]});
            var Q35;
            {var subQ0=sQuery(id+"F1.wireOp",EDGE,"E44.MirrorCS");var subQ1=sQuery(id+"F1.wireOp",EDGE,"E28.19");Q35=makeQuery(id+"F8.boolean.opBoolean","MERGE",EDGE,{"derivedFrom":[makeQuery(id+"F7.boolean.opBoolean","COPY",EDGE,{"derivedFrom":makeQuery(id+"F7.opSweep","SWEPT_EDGE",EDGE,{"disambiguationData":[OSD([subQ1,subQ0,sQuery(id+"F3.wireOp",EDGE,"E57")])]})}),makeQuery(id+"F8.opSweep","SWEPT_EDGE",EDGE,{"disambiguationData":[OSD([subQ1,subQ0,sQuery(id+"F3.wireOp",EDGE,"E55")])]})]});}
            var Q36;
            Q36=makeQuery(id+"F11.opShell","OFFSET_EDGE",EDGE,{"disambiguationData":[OSD([sQuery(id+"F1.wireOp",EDGE,"E28.9"),sQuery(id+"F1.wireOp",EDGE,"E42.MirrorCS"),sQuery(id+"F3.wireOp",EDGE,"E55"),sQuery(id+"F3.wireOp",EDGE,"E57")])]});
            fillet(context, id + "F14", {"entities" : qUnion([Q0, Q1, Q2, Q3, Q4, Q5, Q6, Q7, Q8, Q9, Q10, Q11, Q12, Q13, Q14, Q15, Q16, Q17, Q18, Q19, Q20, Q21, Q22, Q23, Q24, Q25, Q26, Q27, Q28, Q29, Q30, Q31, Q32, Q33, Q34, Q35, Q36]), "radius" : 2 * mm, "allowEdgeOverflow" : false});
        }
        {
            var Q0;
            {var subQ0=sQuery(id+"F3.wireOp",VERTEX,"E55.end");Q0=makeQuery(id+"F13.boolean.opBoolean","MERGE",FACE,{"derivedFrom":[makeQuery(id+"F10.boolean.opBoolean","MERGE",FACE,{"derivedFrom":[makeQuery(id+"F8.boolean.opBoolean","COPY",FACE,{"derivedFrom":makeQuery(id+"F8.opSweep","CAP_FACE",FACE,{"disambiguationData":[OSD([sQuery(id+"F1.wireOp",EDGE,"E28.0"),sQuery(id+"F1.wireOp",EDGE,"E28.1"),sQuery(id+"F1.wireOp",EDGE,"E28.2"),sQuery(id+"F1.wireOp",EDGE,"E28.3"),sQuery(id+"F1.wireOp",EDGE,"E28.5"),sQuery(id+"F1.wireOp",EDGE,"E28.6"),sQuery(id+"F1.wireOp",EDGE,"E28.7"),sQuery(id+"F1.wireOp",EDGE,"E28.8"),sQuery(id+"F1.wireOp",EDGE,"E28.9"),sQuery(id+"F1.wireOp",EDGE,"E28.10"),sQuery(id+"F1.wireOp",EDGE,"E28.11"),sQuery(id+"F1.wireOp",EDGE,"E28.12"),sQuery(id+"F1.wireOp",EDGE,"E28.13"),sQuery(id+"F1.wireOp",EDGE,"E28.14"),sQuery(id+"F1.wireOp",EDGE,"E28.16"),sQuery(id+"F1.wireOp",EDGE,"E28.17"),sQuery(id+"F1.wireOp",EDGE,"E28.18"),sQuery(id+"F1.wireOp",EDGE,"E28.19"),sQuery(id+"F1.wireOp",EDGE,"E29"),sQuery(id+"F1.wireOp",EDGE,"E30"),sQuery(id+"F1.wireOp",EDGE,"E31"),sQuery(id+"F1.wireOp",EDGE,"E32.MirrorCS"),sQuery(id+"F1.wireOp",EDGE,"E33.MirrorCS"),sQuery(id+"F1.wireOp",EDGE,"E34.MirrorCS"),sQuery(id+"F1.wireOp",EDGE,"E35"),sQuery(id+"F1.wireOp",EDGE,"E36"),sQuery(id+"F1.wireOp",EDGE,"E37"),subQ0])],"isStart":false})}),makeQuery(id+"F10.opSweep","CAP_FACE",FACE,{"disambiguationData":[OSD([sQuery(id+"F2.wireOp",EDGE,"E53.bottom"),sQuery(id+"F2.wireOp",EDGE,"E53.top"),sQuery(id+"F2.wireOp",EDGE,"E53.left"),sQuery(id+"F2.wireOp",EDGE,"E53.right"),subQ0])],"isStart":false}),makeQuery(id+"F10.opSweep","CAP_FACE",FACE,{"disambiguationData":[OSD([sQuery(id+"F2.wireOp",EDGE,"E54.bottom"),sQuery(id+"F2.wireOp",EDGE,"E54.top"),sQuery(id+"F2.wireOp",EDGE,"E54.left"),sQuery(id+"F2.wireOp",EDGE,"E54.right"),subQ0])],"isStart":false})]}),makeQuery(id+"F13.opSweep","CAP_FACE",FACE,{"disambiguationData":[OSD([subQ0,sQuery(id+"F12.wireOp",EDGE,"7293b043-83ef-4255-ae6d-b3dc5b9a2924.0"),sQuery(id+"F12.wireOp",EDGE,"7293b043-83ef-4255-ae6d-b3dc5b9a2924.1"),sQuery(id+"F12.wireOp",EDGE,"7293b043-83ef-4255-ae6d-b3dc5b9a2924.2"),sQuery(id+"F12.wireOp",EDGE,"7293b043-83ef-4255-ae6d-b3dc5b9a2924.3"),sQuery(id+"F12.wireOp",EDGE,"7293b043-83ef-4255-ae6d-b3dc5b9a2924.4"),sQuery(id+"F12.wireOp",EDGE,"7293b043-83ef-4255-ae6d-b3dc5b9a2924.5"),sQuery(id+"F12.wireOp",EDGE,"7293b043-83ef-4255-ae6d-b3dc5b9a2924.6"),sQuery(id+"F12.wireOp",EDGE,"7293b043-83ef-4255-ae6d-b3dc5b9a2924.7"),sQuery(id+"F12.wireOp",EDGE,"illqywf3-bTeU-BicJ-eL38-BuILVfbRQocb")])],"isStart":false}),makeQuery(id+"F13.opSweep","CAP_FACE",FACE,{"disambiguationData":[OSD([subQ0,sQuery(id+"F12.wireOp",EDGE,"70b18b86-a124-4c69-b360-074546a5286a0.MirrorCS"),sQuery(id+"F12.wireOp",EDGE,"e57e1a6b-d62b-49b2-a005-49e9c515f2e70.MirrorCS"),sQuery(id+"F12.wireOp",EDGE,"b5c8ba8e-675c-42c0-b8a6-c8ccde90b03b0.MirrorCS"),sQuery(id+"F12.wireOp",EDGE,"2b51d841-ab56-46fc-a233-bf4b134416720.MirrorCS"),sQuery(id+"F12.wireOp",EDGE,"2ce506aa-516a-486f-9163-cfcafb0629370.MirrorCS"),sQuery(id+"F12.wireOp",EDGE,"b170f0c0-2848-43ee-ab32-be4ed6cfa2f00.MirrorCS"),sQuery(id+"F12.wireOp",EDGE,"7071eb6a-4e67-4c53-ad75-c6296ee54e740.MirrorCS"),sQuery(id+"F12.wireOp",EDGE,"bdd4a403-c5b4-428f-abee-52623345626a0.MirrorCS"),sQuery(id+"F12.wireOp",EDGE,"96279677-90b9-4bf5-aae9-6bb9f1e2f9ed0.MirrorCS")])],"isStart":false})]});}
            var sketch = newSketch(context, id + "F15", { "sketchPlane" : qUnion([Q0])});
            skLineSegment(sketch, "E72.0", {"start": v(-29.36, 28.36) * mm, "end": v(-29.36, -28.36) * mm, "construction": true});
            skLineSegment(sketch, "E73.bottom", {"start": v(-29.36, 28.36) * mm, "end": v(-41.36, 28.36) * mm});
            skLineSegment(sketch, "E73.top", {"start": v(-29.36, 27.26) * mm, "end": v(-41.36, 27.26) * mm});
            skLineSegment(sketch, "E73.left", {"start": v(-29.36, 28.36) * mm, "end": v(-29.36, 27.26) * mm});
            skLineSegment(sketch, "E73.right", {"start": v(-41.36, 28.36) * mm, "end": v(-41.36, 27.26) * mm});
            skLineSegment(sketch, "E74.MirrorCS", {"start": v(-41.36, -28.36) * mm, "end": v(-41.36, -27.26) * mm});
            skLineSegment(sketch, "E75.MirrorCS", {"start": v(-29.36, -28.36) * mm, "end": v(-41.36, -28.36) * mm});
            skLineSegment(sketch, "E76.MirrorCS", {"start": v(-29.36, -27.26) * mm, "end": v(-41.36, -27.26) * mm});
            skLineSegment(sketch, "E77.MirrorCS", {"start": v(-29.36, -28.36) * mm, "end": v(-29.36, -27.26) * mm});
            skLineSegment(sketch, "E78.MirrorCS", {"start": v(29.36, 28.36) * mm, "end": v(41.36, 28.36) * mm});
            skLineSegment(sketch, "E79.MirrorCS", {"start": v(41.36, 28.36) * mm, "end": v(41.36, 27.26) * mm});
            skLineSegment(sketch, "E80.MirrorCS", {"start": v(29.36, 27.26) * mm, "end": v(41.36, 27.26) * mm});
            skLineSegment(sketch, "E81.MirrorCS", {"start": v(29.36, 28.36) * mm, "end": v(29.36, 27.26) * mm});
            skLineSegment(sketch, "E82.MirrorCS", {"start": v(29.36, -28.36) * mm, "end": v(29.36, -27.26) * mm});
            skLineSegment(sketch, "E83.MirrorCS", {"start": v(29.36, -27.26) * mm, "end": v(41.36, -27.26) * mm});
            skLineSegment(sketch, "E84.MirrorCS", {"start": v(29.36, -28.36) * mm, "end": v(41.36, -28.36) * mm});
            skLineSegment(sketch, "E85.MirrorCS", {"start": v(41.36, -28.36) * mm, "end": v(41.36, -27.26) * mm});
            skSolve(sketch);
        }
        {
            var Q0;
            Q0=makeQuery(id+"F13.boolean.opBoolean","COPY",EDGE,{"derivedFrom":makeQuery(id+"F13.opSweep","SWEPT_EDGE",EDGE,{"disambiguationData":[OSD([sQuery(id+"F3.wireOp",EDGE,"E58"),sQuery(id+"F12.wireOp",EDGE,"b170f0c0-2848-43ee-ab32-be4ed6cfa2f00.MirrorCS"),sQuery(id+"F12.wireOp",EDGE,"7071eb6a-4e67-4c53-ad75-c6296ee54e740.MirrorCS")])]})});
            var Q1;
            Q1=makeQuery(id+"F13.boolean.opBoolean","COPY",EDGE,{"derivedFrom":makeQuery(id+"F13.opSweep","SWEPT_EDGE",EDGE,{"disambiguationData":[OSD([sQuery(id+"F3.wireOp",EDGE,"E58"),sQuery(id+"F12.wireOp",EDGE,"2ce506aa-516a-486f-9163-cfcafb0629370.MirrorCS"),sQuery(id+"F12.wireOp",EDGE,"b170f0c0-2848-43ee-ab32-be4ed6cfa2f00.MirrorCS")])]})});
            var Q2;
            Q2=makeQuery(id+"F13.boolean.opBoolean","COPY",EDGE,{"derivedFrom":makeQuery(id+"F13.opSweep","SWEPT_EDGE",EDGE,{"disambiguationData":[OSD([sQuery(id+"F3.wireOp",EDGE,"E58"),sQuery(id+"F12.wireOp",EDGE,"7293b043-83ef-4255-ae6d-b3dc5b9a2924.3"),sQuery(id+"F12.wireOp",EDGE,"7293b043-83ef-4255-ae6d-b3dc5b9a2924.7")])]})});
            var Q3;
            Q3=makeQuery(id+"F13.boolean.opBoolean","COPY",EDGE,{"derivedFrom":makeQuery(id+"F13.opSweep","SWEPT_EDGE",EDGE,{"disambiguationData":[OSD([sQuery(id+"F3.wireOp",EDGE,"E58"),sQuery(id+"F12.wireOp",EDGE,"7293b043-83ef-4255-ae6d-b3dc5b9a2924.6"),sQuery(id+"F12.wireOp",EDGE,"7293b043-83ef-4255-ae6d-b3dc5b9a2924.7")])]})});
            var Q4;
            {var subQ0=sQuery(id+"F1.wireOp",EDGE,"E29");var subQ1=sQuery(id+"F1.wireOp",EDGE,"E28.4");var subQ2=sQuery(id+"F1.wireOp",EDGE,"E28.3");Q4=makeQuery(id+"F8.boolean.opBoolean","MERGE",EDGE,{"derivedFrom":[makeQuery(id+"F7.boolean.opBoolean","COPY",EDGE,{"derivedFrom":makeQuery(id+"F7.opSweep","SWEPT_EDGE",EDGE,{"disambiguationData":[OSD([subQ2,subQ1,subQ0,sQuery(id+"F3.wireOp",EDGE,"E57")])]})}),makeQuery(id+"F8.opSweep","SWEPT_EDGE",EDGE,{"disambiguationData":[OSD([subQ2,subQ1,subQ0,sQuery(id+"F3.wireOp",EDGE,"E55")])]})]});}
            var Q5;
            {var subQ0=sQuery(id+"F1.wireOp",EDGE,"E32.MirrorCS");var subQ1=sQuery(id+"F1.wireOp",EDGE,"E28.15");var subQ2=sQuery(id+"F1.wireOp",EDGE,"E28.14");Q5=makeQuery(id+"F8.boolean.opBoolean","MERGE",EDGE,{"derivedFrom":[makeQuery(id+"F7.boolean.opBoolean","COPY",EDGE,{"derivedFrom":makeQuery(id+"F7.opSweep","SWEPT_EDGE",EDGE,{"disambiguationData":[OSD([subQ2,subQ1,subQ0,sQuery(id+"F3.wireOp",EDGE,"E57")])]})}),makeQuery(id+"F8.opSweep","SWEPT_EDGE",EDGE,{"disambiguationData":[OSD([subQ2,subQ1,subQ0,sQuery(id+"F3.wireOp",EDGE,"E55")])]})]});}
            var Q6;
            {var subQ0=sQuery(id+"F1.wireOp",EDGE,"E34.MirrorCS");var subQ1=sQuery(id+"F1.wireOp",EDGE,"E28.16");var subQ2=sQuery(id+"F1.wireOp",EDGE,"E28.15");Q6=makeQuery(id+"F8.boolean.opBoolean","MERGE",EDGE,{"derivedFrom":[makeQuery(id+"F7.boolean.opBoolean","COPY",EDGE,{"derivedFrom":makeQuery(id+"F7.opSweep","SWEPT_EDGE",EDGE,{"disambiguationData":[OSD([subQ2,subQ1,subQ0,sQuery(id+"F3.wireOp",EDGE,"E57")])]})}),makeQuery(id+"F8.opSweep","SWEPT_EDGE",EDGE,{"disambiguationData":[OSD([subQ2,subQ1,subQ0,sQuery(id+"F3.wireOp",EDGE,"E55")])]})]});}
            var Q7;
            {var subQ0=sQuery(id+"F1.wireOp",EDGE,"E31");var subQ1=sQuery(id+"F1.wireOp",EDGE,"E28.6");var subQ2=sQuery(id+"F1.wireOp",EDGE,"E28.4");Q7=makeQuery(id+"F8.boolean.opBoolean","MERGE",EDGE,{"derivedFrom":[makeQuery(id+"F7.boolean.opBoolean","COPY",EDGE,{"derivedFrom":makeQuery(id+"F7.opSweep","SWEPT_EDGE",EDGE,{"disambiguationData":[OSD([subQ2,subQ1,subQ0,sQuery(id+"F3.wireOp",EDGE,"E57")])]})}),makeQuery(id+"F8.opSweep","SWEPT_EDGE",EDGE,{"disambiguationData":[OSD([subQ2,subQ1,subQ0,sQuery(id+"F3.wireOp",EDGE,"E55")])]})]});}
            var Q8;
            {var subQ0=sQuery(id+"F1.wireOp",EDGE,"E33.MirrorCS");var subQ1=sQuery(id+"F1.wireOp",EDGE,"E32.MirrorCS");Q8=makeQuery(id+"F8.boolean.opBoolean","MERGE",EDGE,{"derivedFrom":[makeQuery(id+"F7.boolean.opBoolean","COPY",EDGE,{"derivedFrom":makeQuery(id+"F7.opSweep","SWEPT_EDGE",EDGE,{"disambiguationData":[OSD([subQ1,subQ0,sQuery(id+"F3.wireOp",EDGE,"E57")])]})}),makeQuery(id+"F8.opSweep","SWEPT_EDGE",EDGE,{"disambiguationData":[OSD([subQ1,subQ0,sQuery(id+"F3.wireOp",EDGE,"E55")])]})]});}
            var Q9;
            {var subQ0=sQuery(id+"F1.wireOp",EDGE,"E34.MirrorCS");var subQ1=sQuery(id+"F1.wireOp",EDGE,"E33.MirrorCS");Q9=makeQuery(id+"F8.boolean.opBoolean","MERGE",EDGE,{"derivedFrom":[makeQuery(id+"F7.boolean.opBoolean","COPY",EDGE,{"derivedFrom":makeQuery(id+"F7.opSweep","SWEPT_EDGE",EDGE,{"disambiguationData":[OSD([subQ1,subQ0,sQuery(id+"F3.wireOp",EDGE,"E57")])]})}),makeQuery(id+"F8.opSweep","SWEPT_EDGE",EDGE,{"disambiguationData":[OSD([subQ1,subQ0,sQuery(id+"F3.wireOp",EDGE,"E55")])]})]});}
            var Q10;
            {var subQ0=sQuery(id+"F1.wireOp",EDGE,"E30");var subQ1=sQuery(id+"F1.wireOp",EDGE,"E29");Q10=makeQuery(id+"F8.boolean.opBoolean","MERGE",EDGE,{"derivedFrom":[makeQuery(id+"F7.boolean.opBoolean","COPY",EDGE,{"derivedFrom":makeQuery(id+"F7.opSweep","SWEPT_EDGE",EDGE,{"disambiguationData":[OSD([subQ1,subQ0,sQuery(id+"F3.wireOp",EDGE,"E57")])]})}),makeQuery(id+"F8.opSweep","SWEPT_EDGE",EDGE,{"disambiguationData":[OSD([subQ1,subQ0,sQuery(id+"F3.wireOp",EDGE,"E55")])]})]});}
            var Q11;
            {var subQ0=sQuery(id+"F1.wireOp",EDGE,"E31");var subQ1=sQuery(id+"F1.wireOp",EDGE,"E30");Q11=makeQuery(id+"F8.boolean.opBoolean","MERGE",EDGE,{"derivedFrom":[makeQuery(id+"F7.boolean.opBoolean","COPY",EDGE,{"derivedFrom":makeQuery(id+"F7.opSweep","SWEPT_EDGE",EDGE,{"disambiguationData":[OSD([subQ1,subQ0,sQuery(id+"F3.wireOp",EDGE,"E57")])]})}),makeQuery(id+"F8.opSweep","SWEPT_EDGE",EDGE,{"disambiguationData":[OSD([subQ1,subQ0,sQuery(id+"F3.wireOp",EDGE,"E55")])]})]});}
            var Q12;
            Q12=makeQuery(id+"F13.boolean.opBoolean","COPY",EDGE,{"derivedFrom":makeQuery(id+"F13.opSweep","SWEPT_EDGE",EDGE,{"disambiguationData":[OSD([sQuery(id+"F2.wireOp",EDGE,"E53.left"),sQuery(id+"F3.wireOp",VERTEX,"E58.end"),sQuery(id+"F3.wireOp",EDGE,"E58"),sQuery(id+"F12.wireOp",EDGE,"7293b043-83ef-4255-ae6d-b3dc5b9a2924.4"),sQuery(id+"F12.wireOp",EDGE,"illqywf3-bTeU-BicJ-eL38-BuILVfbRQocb")])]})});
            var Q13;
            {var subQ0=sQuery(id+"F3.wireOp",EDGE,"E55");var subQ1=sQuery(id+"F1.wireOp",EDGE,"E28.7");Q13=makeQuery(id+"F10.boolean.opBoolean","INTERSECT",EDGE,{"derivedFrom":[makeQuery(id+"F8.boolean.opBoolean","MERGE",FACE,{"derivedFrom":[makeQuery(id+"F7.boolean.opBoolean","COPY",FACE,{"derivedFrom":makeQuery(id+"F7.opSweep","SWEPT_FACE",FACE,{"disambiguationData":[OSD([subQ1,sQuery(id+"F3.wireOp",EDGE,"E57")])]})}),makeQuery(id+"F8.opSweep","SWEPT_FACE",FACE,{"disambiguationData":[OSD([subQ1,subQ0])]})]}),makeQuery(id+"F10.opSweep","SWEPT_FACE",FACE,{"disambiguationData":[OSD([sQuery(id+"F2.wireOp",EDGE,"E53.left"),subQ0])]})]});}
            var Q14;
            {var subQ0=sQuery(id+"F3.wireOp",EDGE,"E55");var subQ1=sQuery(id+"F1.wireOp",EDGE,"E28.1");Q14=makeQuery(id+"F10.boolean.opBoolean","INTERSECT",EDGE,{"derivedFrom":[makeQuery(id+"F8.boolean.opBoolean","MERGE",FACE,{"derivedFrom":[makeQuery(id+"F7.boolean.opBoolean","COPY",FACE,{"derivedFrom":makeQuery(id+"F7.opSweep","SWEPT_FACE",FACE,{"disambiguationData":[OSD([subQ1,sQuery(id+"F3.wireOp",EDGE,"E57")])]})}),makeQuery(id+"F8.opSweep","SWEPT_FACE",FACE,{"disambiguationData":[OSD([subQ1,subQ0])]})]}),makeQuery(id+"F10.opSweep","SWEPT_FACE",FACE,{"disambiguationData":[OSD([sQuery(id+"F2.wireOp",EDGE,"E53.left"),subQ0])]})]});}
            var Q15;
            Q15=makeQuery(id+"F13.boolean.opBoolean","COPY",EDGE,{"derivedFrom":makeQuery(id+"F13.opSweep","SWEPT_EDGE",EDGE,{"disambiguationData":[OSD([sQuery(id+"F2.wireOp",EDGE,"E53.left"),sQuery(id+"F3.wireOp",VERTEX,"E58.end"),sQuery(id+"F3.wireOp",EDGE,"E58"),sQuery(id+"F12.wireOp",EDGE,"7293b043-83ef-4255-ae6d-b3dc5b9a2924.0"),sQuery(id+"F12.wireOp",EDGE,"illqywf3-bTeU-BicJ-eL38-BuILVfbRQocb")])]})});
            var Q16;
            Q16=makeQuery(id+"F13.boolean.opBoolean","COPY",EDGE,{"derivedFrom":makeQuery(id+"F13.opSweep","SWEPT_EDGE",EDGE,{"disambiguationData":[OSD([sQuery(id+"F3.wireOp",EDGE,"E58"),sQuery(id+"F12.wireOp",EDGE,"70b18b86-a124-4c69-b360-074546a5286a0.MirrorCS"),sQuery(id+"F12.wireOp",EDGE,"96279677-90b9-4bf5-aae9-6bb9f1e2f9ed0.MirrorCS")])]})});
            var Q17;
            {var subQ0=sQuery(id+"F3.wireOp",EDGE,"E55");var subQ1=sQuery(id+"F1.wireOp",EDGE,"E28.11");Q17=makeQuery(id+"F10.boolean.opBoolean","INTERSECT",EDGE,{"derivedFrom":[makeQuery(id+"F8.boolean.opBoolean","MERGE",FACE,{"derivedFrom":[makeQuery(id+"F7.boolean.opBoolean","COPY",FACE,{"derivedFrom":makeQuery(id+"F7.opSweep","SWEPT_FACE",FACE,{"disambiguationData":[OSD([subQ1,sQuery(id+"F3.wireOp",EDGE,"E57")])]})}),makeQuery(id+"F8.opSweep","SWEPT_FACE",FACE,{"disambiguationData":[OSD([subQ1,subQ0])]})]}),makeQuery(id+"F10.opSweep","SWEPT_FACE",FACE,{"disambiguationData":[OSD([sQuery(id+"F2.wireOp",EDGE,"E54.right"),subQ0])]})]});}
            var Q18;
            Q18=makeQuery(id+"F13.boolean.opBoolean","COPY",EDGE,{"derivedFrom":makeQuery(id+"F13.opSweep","SWEPT_EDGE",EDGE,{"disambiguationData":[OSD([sQuery(id+"F3.wireOp",EDGE,"E58"),sQuery(id+"F12.wireOp",EDGE,"70b18b86-a124-4c69-b360-074546a5286a0.MirrorCS"),sQuery(id+"F12.wireOp",EDGE,"e57e1a6b-d62b-49b2-a005-49e9c515f2e70.MirrorCS")])]})});
            fillet(context, id + "F16", {"entities" : qUnion([Q0, Q1, Q2, Q3, Q4, Q5, Q6, Q7, Q8, Q9, Q10, Q11, Q12, Q13, Q14, Q15, Q16, Q17, Q18]), "radius" : .5 * mm, "allowEdgeOverflow" : false});
        }
        {
            var Q0;
            {var subQ1=sQuery(id+"F1.wireOp",EDGE,"E31");var subQ3=sQuery(id+"F2.wireOp",EDGE,"E54.top");var subQ5=sQuery(id+"F1.wireOp",EDGE,"E30");var subQ6=sQuery(id+"F1.wireOp",EDGE,"E37");var subQ7=sQuery(id+"F2.wireOp",EDGE,"E54.bottom");var subQ9=sQuery(id+"F1.wireOp",EDGE,"E29");var subQ10=sQuery(id+"F1.wireOp",EDGE,"E36");var subQ11=sQuery(id+"F2.wireOp",EDGE,"E53.top");var subQ13=sQuery(id+"F1.wireOp",EDGE,"E28.18");var subQ15=sQuery(id+"F1.wireOp",EDGE,"E35");var subQ16=sQuery(id+"F2.wireOp",EDGE,"E53.bottom");var subQ18=sQuery(id+"F1.wireOp",EDGE,"E28.17");var subQ19=sQuery(id+"F1.wireOp",EDGE,"E34.MirrorCS");var subQ20=sQuery(id+"F1.wireOp",EDGE,"E28.16");var subQ21=sQuery(id+"F1.wireOp",EDGE,"E33.MirrorCS");var subQ22=sQuery(id+"F1.wireOp",EDGE,"E28.14");var subQ23=sQuery(id+"F1.wireOp",EDGE,"E32.MirrorCS");var subQ24=sQuery(id+"F1.wireOp",EDGE,"E28.13");var subQ26=sQuery(id+"F1.wireOp",EDGE,"E28.12");var subQ28=sQuery(id+"F1.wireOp",EDGE,"E28.11");var subQ29=sQuery(id+"F1.wireOp",EDGE,"E28.10");var subQ31=sQuery(id+"F1.wireOp",EDGE,"E28.19");var subQ32=sQuery(id+"F1.wireOp",EDGE,"E28.9");var subQ34=sQuery(id+"F1.wireOp",EDGE,"E28.8");var subQ36=sQuery(id+"F1.wireOp",EDGE,"E28.7");var subQ37=sQuery(id+"F1.wireOp",EDGE,"E28.6");var subQ39=sQuery(id+"F1.wireOp",EDGE,"E28.5");var subQ42=sQuery(id+"F1.wireOp",EDGE,"E28.3");var subQ43=sQuery(id+"F1.wireOp",EDGE,"E28.2");var subQ44=sQuery(id+"F1.wireOp",EDGE,"E28.1");var subQ46=sQuery(id+"F1.wireOp",EDGE,"E28.0");var subQ52=sQuery(id+"F2.wireOp",EDGE,"E53.right");var subQ53=sQuery(id+"F2.wireOp",EDGE,"E53.left");var subQ58=sQuery(id+"F2.wireOp",EDGE,"E54.right");var subQ59=sQuery(id+"F2.wireOp",EDGE,"E54.left");var subQ66=sQuery(id+"F3.wireOp",VERTEX,"E55.end");Q0=makeQuery(id+"FbqidZFr9ypFAgr_1.boolean.opBoolean","SPLIT",FACE,{"disambiguationData":[TD([makeQuery(id+"FbqidZFr9ypFAgr_1.opExtrude","SWEPT_FACE",FACE,{"disambiguationData":[OSD([sQuery(id+"F15.wireOp",EDGE,"CY3hGOyY-NcrF-lk1t-4vKU-rVBS9GiHpt78.bottom")])]})])],"derivedFrom":makeQuery(id+"F13.boolean.opBoolean","MERGE",FACE,{"derivedFrom":[makeQuery(id+"F10.boolean.opBoolean","MERGE",FACE,{"derivedFrom":[makeQuery(id+"F8.boolean.opBoolean","COPY",FACE,{"derivedFrom":makeQuery(id+"F8.opSweep","CAP_FACE",FACE,{"disambiguationData":[OSD([subQ46,subQ44,subQ43,subQ42,subQ39,subQ37,subQ36,subQ34,subQ32,subQ29,subQ28,subQ26,subQ24,subQ22,subQ20,subQ18,subQ13,subQ31,subQ9,subQ5,subQ1,subQ23,subQ21,subQ19,subQ15,subQ10,subQ6,subQ66])],"isStart":false})}),makeQuery(id+"F10.opSweep","CAP_FACE",FACE,{"disambiguationData":[OSD([subQ16,subQ11,subQ53,subQ52,subQ66])],"isStart":false}),makeQuery(id+"F10.opSweep","CAP_FACE",FACE,{"disambiguationData":[OSD([subQ7,subQ3,subQ59,subQ58,subQ66])],"isStart":false})]}),makeQuery(id+"F13.opSweep","CAP_FACE",FACE,{"disambiguationData":[OSD([subQ66,sQuery(id+"F12.wireOp",EDGE,"7293b043-83ef-4255-ae6d-b3dc5b9a2924.0"),sQuery(id+"F12.wireOp",EDGE,"7293b043-83ef-4255-ae6d-b3dc5b9a2924.1"),sQuery(id+"F12.wireOp",EDGE,"7293b043-83ef-4255-ae6d-b3dc5b9a2924.2"),sQuery(id+"F12.wireOp",EDGE,"7293b043-83ef-4255-ae6d-b3dc5b9a2924.3"),sQuery(id+"F12.wireOp",EDGE,"7293b043-83ef-4255-ae6d-b3dc5b9a2924.4"),sQuery(id+"F12.wireOp",EDGE,"7293b043-83ef-4255-ae6d-b3dc5b9a2924.5"),sQuery(id+"F12.wireOp",EDGE,"7293b043-83ef-4255-ae6d-b3dc5b9a2924.6"),sQuery(id+"F12.wireOp",EDGE,"7293b043-83ef-4255-ae6d-b3dc5b9a2924.7"),sQuery(id+"F12.wireOp",EDGE,"illqywf3-bTeU-BicJ-eL38-BuILVfbRQocb")])],"isStart":false}),makeQuery(id+"F13.opSweep","CAP_FACE",FACE,{"disambiguationData":[OSD([subQ66,sQuery(id+"F12.wireOp",EDGE,"70b18b86-a124-4c69-b360-074546a5286a0.MirrorCS"),sQuery(id+"F12.wireOp",EDGE,"e57e1a6b-d62b-49b2-a005-49e9c515f2e70.MirrorCS"),sQuery(id+"F12.wireOp",EDGE,"b5c8ba8e-675c-42c0-b8a6-c8ccde90b03b0.MirrorCS"),sQuery(id+"F12.wireOp",EDGE,"2b51d841-ab56-46fc-a233-bf4b134416720.MirrorCS"),sQuery(id+"F12.wireOp",EDGE,"2ce506aa-516a-486f-9163-cfcafb0629370.MirrorCS"),sQuery(id+"F12.wireOp",EDGE,"b170f0c0-2848-43ee-ab32-be4ed6cfa2f00.MirrorCS"),sQuery(id+"F12.wireOp",EDGE,"7071eb6a-4e67-4c53-ad75-c6296ee54e740.MirrorCS"),sQuery(id+"F12.wireOp",EDGE,"bdd4a403-c5b4-428f-abee-52623345626a0.MirrorCS"),sQuery(id+"F12.wireOp",EDGE,"96279677-90b9-4bf5-aae9-6bb9f1e2f9ed0.MirrorCS")])],"isStart":false})]})});}
            var Q1;
            Q1=makeQuery(id+"F11.opShell","OFFSET_FACE",FACE,{"disambiguationData":[OSD([sQuery(id+"F3.wireOp",VERTEX,"E56.end"),sQuery(id+"F4.wireOp",EDGE,"E61.bottom"),sQuery(id+"F4.wireOp",EDGE,"E61.top"),sQuery(id+"F4.wireOp",EDGE,"E61.left"),sQuery(id+"F4.wireOp",EDGE,"E61.right")]),OD(1.0)]});
            var Q2;
            Q2=makeQuery(id+"F11.opShell","OFFSET_FACE",FACE,{"disambiguationData":[OSD([sQuery(id+"F3.wireOp",VERTEX,"E56.end"),sQuery(id+"F4.wireOp",EDGE,"E61.bottom"),sQuery(id+"F4.wireOp",EDGE,"E61.top"),sQuery(id+"F4.wireOp",EDGE,"E61.left"),sQuery(id+"F4.wireOp",EDGE,"E61.right")]),OD(0.0)]});
            var Q3;
            {var subQ1=sQuery(id+"F2.wireOp",EDGE,"E53.left");var subQ2=sQuery(id+"F2.wireOp",EDGE,"E53.right");var subQ3=sQuery(id+"F1.wireOp",EDGE,"E28.0");var subQ5=sQuery(id+"F1.wireOp",EDGE,"E28.8");var subQ6=sQuery(id+"F2.wireOp",EDGE,"E53.top");var subQ7=sQuery(id+"F2.wireOp",EDGE,"E53.bottom");var subQ10=sQuery(id+"F1.wireOp",EDGE,"E28.1");var subQ11=sQuery(id+"F1.wireOp",EDGE,"E28.7");var subQ12=sQuery(id+"F3.wireOp",VERTEX,"E55.end");Q3=makeQuery(id+"FbqidZFr9ypFAgr_1.boolean.opBoolean","SPLIT",FACE,{"disambiguationData":[TD([makeQuery(id+"FbqidZFr9ypFAgr_1.opExtrude","SWEPT_FACE",FACE,{"disambiguationData":[OSD([sQuery(id+"F15.wireOp",EDGE,"CY3hGOyY-NcrF-lk1t-4vKU-rVBS9GiHpt78.top")])]})])],"derivedFrom":makeQuery(id+"F10.boolean.opBoolean","MERGE",FACE,{"derivedFrom":[makeQuery(id+"F8.boolean.opBoolean","COPY",FACE,{"derivedFrom":makeQuery(id+"F8.opSweep","CAP_FACE",FACE,{"disambiguationData":[OSD([subQ3,subQ10,sQuery(id+"F1.wireOp",EDGE,"E28.2"),sQuery(id+"F1.wireOp",EDGE,"E28.3"),sQuery(id+"F1.wireOp",EDGE,"E28.5"),sQuery(id+"F1.wireOp",EDGE,"E28.6"),subQ11,subQ5,sQuery(id+"F1.wireOp",EDGE,"E28.9"),sQuery(id+"F1.wireOp",EDGE,"E28.10"),sQuery(id+"F1.wireOp",EDGE,"E28.11"),sQuery(id+"F1.wireOp",EDGE,"E28.12"),sQuery(id+"F1.wireOp",EDGE,"E28.13"),sQuery(id+"F1.wireOp",EDGE,"E28.14"),sQuery(id+"F1.wireOp",EDGE,"E28.16"),sQuery(id+"F1.wireOp",EDGE,"E28.17"),sQuery(id+"F1.wireOp",EDGE,"E28.18"),sQuery(id+"F1.wireOp",EDGE,"E28.19"),sQuery(id+"F1.wireOp",EDGE,"E29"),sQuery(id+"F1.wireOp",EDGE,"E30"),sQuery(id+"F1.wireOp",EDGE,"E31"),sQuery(id+"F1.wireOp",EDGE,"E32.MirrorCS"),sQuery(id+"F1.wireOp",EDGE,"E33.MirrorCS"),sQuery(id+"F1.wireOp",EDGE,"E34.MirrorCS"),sQuery(id+"F1.wireOp",EDGE,"E35"),sQuery(id+"F1.wireOp",EDGE,"E36"),sQuery(id+"F1.wireOp",EDGE,"E37"),subQ12])],"isStart":false})}),makeQuery(id+"F10.opSweep","CAP_FACE",FACE,{"disambiguationData":[OSD([subQ7,subQ6,subQ1,subQ2,subQ12])],"isStart":false}),makeQuery(id+"F10.opSweep","CAP_FACE",FACE,{"disambiguationData":[OSD([sQuery(id+"F2.wireOp",EDGE,"E54.bottom"),sQuery(id+"F2.wireOp",EDGE,"E54.top"),sQuery(id+"F2.wireOp",EDGE,"E54.left"),sQuery(id+"F2.wireOp",EDGE,"E54.right"),subQ12])],"isStart":false})]})});}
            var Q4;
            Q4=makeQuery(id+"F13.boolean.opBoolean","COPY",FACE,{"derivedFrom":makeQuery(id+"F13.opSweep","CAP_FACE",FACE,{"disambiguationData":[OSD([sQuery(id+"F3.wireOp",VERTEX,"E55.end"),sQuery(id+"F12.wireOp",EDGE,"e57e1a6b-d62b-49b2-a005-49e9c515f2e70.MirrorCS"),sQuery(id+"F12.wireOp",EDGE,"b5c8ba8e-675c-42c0-b8a6-c8ccde90b03b0.MirrorCS"),sQuery(id+"F12.wireOp",EDGE,"2b51d841-ab56-46fc-a233-bf4b134416720.MirrorCS"),sQuery(id+"F12.wireOp",EDGE,"2ce506aa-516a-486f-9163-cfcafb0629370.MirrorCS"),sQuery(id+"F12.wireOp",EDGE,"b170f0c0-2848-43ee-ab32-be4ed6cfa2f00.MirrorCS"),sQuery(id+"F12.wireOp",EDGE,"7071eb6a-4e67-4c53-ad75-c6296ee54e740.MirrorCS"),sQuery(id+"F12.wireOp",EDGE,"bdd4a403-c5b4-428f-abee-52623345626a0.MirrorCS"),sQuery(id+"F12.wireOp",EDGE,"96279677-90b9-4bf5-aae9-6bb9f1e2f9ed0.MirrorCS"),sQuery(id+"F12.wireOp",EDGE,"3d8ba52f-ba84-4df5-aa56-e8d0c0cd4fd30.MirrorCS")])],"isStart":false})});
            var Q5;
            {var subQ1=sQuery(id+"F2.wireOp",EDGE,"E54.left");var subQ2=sQuery(id+"F1.wireOp",EDGE,"E28.11");var subQ4=sQuery(id+"F1.wireOp",EDGE,"E28.17");var subQ6=sQuery(id+"F2.wireOp",EDGE,"E54.right");var subQ7=sQuery(id+"F2.wireOp",EDGE,"E54.top");var subQ8=sQuery(id+"F2.wireOp",EDGE,"E54.bottom");var subQ10=sQuery(id+"F1.wireOp",EDGE,"E28.12");var subQ11=sQuery(id+"F1.wireOp",EDGE,"E28.18");var subQ12=sQuery(id+"F3.wireOp",VERTEX,"E55.end");Q5=makeQuery(id+"FbqidZFr9ypFAgr_1.boolean.opBoolean","SPLIT",FACE,{"disambiguationData":[TD([makeQuery(id+"FbqidZFr9ypFAgr_1.opExtrude","SWEPT_FACE",FACE,{"disambiguationData":[OSD([sQuery(id+"F15.wireOp",EDGE,"c200d8bc-39f5-441f-9ce5-a0bf028d987c0.MirrorCS")])]})])],"derivedFrom":makeQuery(id+"F10.boolean.opBoolean","MERGE",FACE,{"derivedFrom":[makeQuery(id+"F8.boolean.opBoolean","COPY",FACE,{"derivedFrom":makeQuery(id+"F8.opSweep","CAP_FACE",FACE,{"disambiguationData":[OSD([sQuery(id+"F1.wireOp",EDGE,"E28.0"),sQuery(id+"F1.wireOp",EDGE,"E28.1"),sQuery(id+"F1.wireOp",EDGE,"E28.2"),sQuery(id+"F1.wireOp",EDGE,"E28.3"),sQuery(id+"F1.wireOp",EDGE,"E28.5"),sQuery(id+"F1.wireOp",EDGE,"E28.6"),sQuery(id+"F1.wireOp",EDGE,"E28.7"),sQuery(id+"F1.wireOp",EDGE,"E28.8"),sQuery(id+"F1.wireOp",EDGE,"E28.9"),sQuery(id+"F1.wireOp",EDGE,"E28.10"),subQ2,subQ10,sQuery(id+"F1.wireOp",EDGE,"E28.13"),sQuery(id+"F1.wireOp",EDGE,"E28.14"),sQuery(id+"F1.wireOp",EDGE,"E28.16"),subQ4,subQ11,sQuery(id+"F1.wireOp",EDGE,"E28.19"),sQuery(id+"F1.wireOp",EDGE,"E29"),sQuery(id+"F1.wireOp",EDGE,"E30"),sQuery(id+"F1.wireOp",EDGE,"E31"),sQuery(id+"F1.wireOp",EDGE,"E32.MirrorCS"),sQuery(id+"F1.wireOp",EDGE,"E33.MirrorCS"),sQuery(id+"F1.wireOp",EDGE,"E34.MirrorCS"),sQuery(id+"F1.wireOp",EDGE,"E35"),sQuery(id+"F1.wireOp",EDGE,"E36"),sQuery(id+"F1.wireOp",EDGE,"E37"),subQ12])],"isStart":false})}),makeQuery(id+"F10.opSweep","CAP_FACE",FACE,{"disambiguationData":[OSD([sQuery(id+"F2.wireOp",EDGE,"E53.bottom"),sQuery(id+"F2.wireOp",EDGE,"E53.top"),sQuery(id+"F2.wireOp",EDGE,"E53.left"),sQuery(id+"F2.wireOp",EDGE,"E53.right"),subQ12])],"isStart":false}),makeQuery(id+"F10.opSweep","CAP_FACE",FACE,{"disambiguationData":[OSD([subQ8,subQ7,subQ1,subQ6,subQ12])],"isStart":false})]})});}
            var Q6;
            Q6=makeQuery(id+"F13.boolean.opBoolean","COPY",FACE,{"derivedFrom":makeQuery(id+"F13.opSweep","CAP_FACE",FACE,{"disambiguationData":[OSD([sQuery(id+"F3.wireOp",VERTEX,"E55.end"),sQuery(id+"F12.wireOp",EDGE,"7293b043-83ef-4255-ae6d-b3dc5b9a2924.0"),sQuery(id+"F12.wireOp",EDGE,"7293b043-83ef-4255-ae6d-b3dc5b9a2924.1"),sQuery(id+"F12.wireOp",EDGE,"7293b043-83ef-4255-ae6d-b3dc5b9a2924.2"),sQuery(id+"F12.wireOp",EDGE,"7293b043-83ef-4255-ae6d-b3dc5b9a2924.3"),sQuery(id+"F12.wireOp",EDGE,"7293b043-83ef-4255-ae6d-b3dc5b9a2924.4"),sQuery(id+"F12.wireOp",EDGE,"7293b043-83ef-4255-ae6d-b3dc5b9a2924.5"),sQuery(id+"F12.wireOp",EDGE,"7293b043-83ef-4255-ae6d-b3dc5b9a2924.6"),sQuery(id+"F12.wireOp",EDGE,"7293b043-83ef-4255-ae6d-b3dc5b9a2924.7"),sQuery(id+"F12.wireOp",EDGE,"6eaf7242-808e-452b-8d9a-fbae19f0b6b7.0")])],"isStart":false})});
            fillet(context, id + "F17", {"entities" : qUnion([Q0, Q1, Q2, Q3, Q4, Q5, Q6]), "radius" : 1 * mm, "allowEdgeOverflow" : false});
        }
        {
            var Q0;
            {var subQ5=sQuery(id+"F3.wireOp",EDGE,"E57");var subQ10=sQuery(id+"F4.wireOp",EDGE,"E61.right");var subQ11=sQuery(id+"F4.wireOp",EDGE,"E61.left");var subQ13=sQuery(id+"F4.wireOp",EDGE,"E61.top");var subQ15=sQuery(id+"F4.wireOp",EDGE,"E61.bottom");Q0=makeQuery(id+"F9.boolean.opBoolean","SPLIT",FACE,{"disambiguationData":[TD([makeQuery(id+"F5.opSweep","SWEPT_FACE",FACE,{"disambiguationData":[OSD([subQ5,subQ15])]})])],"derivedFrom":makeQuery(id+"F5.opSweep","CAP_FACE",FACE,{"disambiguationData":[OSD([sQuery(id+"F3.wireOp",VERTEX,"E58.end"),subQ15,subQ13,subQ11,subQ10])],"isStart":false})});}
            var sketch = newSketch(context, id + "F18", { "sketchPlane" : qUnion([Q0])});
            skArc(sketch, "E86.0", {"start": v(43.3, 69.5) * mm, "mid": v(43.07, 70.07) * mm, "end": v(42.5, 70.3) * mm});
            skLineSegment(sketch, "E86.1", {"start": v(43.3, -69.5) * mm, "end": v(43.3, -15) * mm});
            skLineSegment(sketch, "E86.2", {"start": v(42.5, 70.3) * mm, "end": v(12.5, 70.3) * mm});
            skArc(sketch, "E86.3", {"start": v(42.5, -70.3) * mm, "mid": v(43.07, -70.07) * mm, "end": v(43.3, -69.5) * mm});
            skArc(sketch, "E86.4", {"start": v(-42.5, 70.3) * mm, "mid": v(-43.07, 70.07) * mm, "end": v(-43.3, 69.5) * mm});
            skLineSegment(sketch, "E86.5", {"start": v(-43.3, 69.5) * mm, "end": v(-43.3, 15) * mm});
            skArc(sketch, "E86.6", {"start": v(-43.3, -69.5) * mm, "mid": v(-43.07, -70.07) * mm, "end": v(-42.5, -70.3) * mm});
            skLineSegment(sketch, "E86.7", {"start": v(-42.5, -70.3) * mm, "end": v(-12.5, -70.3) * mm});
            skLineSegment(sketch, "E87", {"start": v(-12.5, 70.3) * mm, "end": v(-12.5, 70.3) * mm});
            skLineSegment(sketch, "E88", {"start": v(12.5, 70.3) * mm, "end": v(12.5, 70.3) * mm});
            skLineSegment(sketch, "E89", {"start": v(-12.5, 71.5) * mm, "end": v(12.5, 71.5) * mm});
            skLineSegment(sketch, "E90.MirrorCS", {"start": v(-12.5, -71.5) * mm, "end": v(12.5, -71.5) * mm});
            skLineSegment(sketch, "E91.MirrorCS", {"start": v(-12.5, -70.3) * mm, "end": v(-12.5, -71.5) * mm});
            skLineSegment(sketch, "E92.MirrorCS", {"start": v(12.5, -70.3) * mm, "end": v(12.5, -71.5) * mm});
            skLineSegment(sketch, "E93", {"start": v(-43.3, 15) * mm, "end": v(-44.5, 15) * mm});
            skLineSegment(sketch, "E94", {"start": v(-44.5, 15) * mm, "end": v(-44.5, -15) * mm});
            skLineSegment(sketch, "E95", {"start": v(-44.5, -15) * mm, "end": v(-43.3, -15) * mm});
            skLineSegment(sketch, "E96.MirrorCS", {"start": v(44.5, 15) * mm, "end": v(44.5, -15) * mm});
            skLineSegment(sketch, "E97.MirrorCS", {"start": v(43.3, 15) * mm, "end": v(44.5, 15) * mm});
            skLineSegment(sketch, "E98.MirrorCS", {"start": v(44.5, -15) * mm, "end": v(43.3, -15) * mm});
            skLineSegment(sketch, "E99", {"start": v(-12.5, 70.3) * mm, "end": v(-12.5, 71.5) * mm});
            skLineSegment(sketch, "E100", {"start": v(12.5, 70.3) * mm, "end": v(12.5, 71.5) * mm});
            skLineSegment(sketch, "E101", {"start": v(-12.5, -70.3) * mm, "end": v(12.5, -70.3) * mm});
            skLineSegment(sketch, "E102", {"start": v(12.5, -70.3) * mm, "end": v(42.5, -70.3) * mm});
            skLineSegment(sketch, "E103", {"start": v(-43.3, -15) * mm, "end": v(-43.3, -69.5) * mm});
            skLineSegment(sketch, "E104", {"start": v(-43.3, 15) * mm, "end": v(-43.3, -15) * mm});
            skLineSegment(sketch, "E105", {"start": v(43.3, 15) * mm, "end": v(43.3, 69.5) * mm});
            skLineSegment(sketch, "E106", {"start": v(43.3, -15) * mm, "end": v(43.3, 15) * mm});
            skLineSegment(sketch, "E107", {"start": v(-12.5, 70.3) * mm, "end": v(-42.5, 70.3) * mm});
            skLineSegment(sketch, "E108", {"start": v(12.5, 70.3) * mm, "end": v(-12.5, 70.3) * mm});
            skSolve(sketch);
        }
        {
            var Q0;
            {var subQ5=sQuery(id+"F3.wireOp",EDGE,"E57");var subQ10=sQuery(id+"F4.wireOp",EDGE,"E61.right");var subQ11=sQuery(id+"F4.wireOp",EDGE,"E61.left");var subQ13=sQuery(id+"F4.wireOp",EDGE,"E61.top");var subQ15=sQuery(id+"F4.wireOp",EDGE,"E61.bottom");Q0=makeQuery(id+"F9.boolean.opBoolean","SPLIT",FACE,{"disambiguationData":[TD([makeQuery(id+"F5.opSweep","SWEPT_FACE",FACE,{"disambiguationData":[OSD([subQ5,subQ15])]})])],"derivedFrom":makeQuery(id+"F5.opSweep","CAP_FACE",FACE,{"disambiguationData":[OSD([sQuery(id+"F3.wireOp",VERTEX,"E58.end"),subQ15,subQ13,subQ11,subQ10])],"isStart":false})});}
            var sketch = newSketch(context, id + "F19", { "sketchPlane" : qUnion([Q0])});
            skLineSegment(sketch, "E109.0", {"start": v(-12.6, 69.9) * mm, "end": v(-12.6, 71.1) * mm});
            skLineSegment(sketch, "E109.1", {"start": v(12.6, -69.9) * mm, "end": v(42.5, -69.9) * mm});
            skArc(sketch, "E109.2", {"start": v(42.5, -69.9) * mm, "mid": v(43.14, -69.64) * mm, "end": v(43.4, -69) * mm});
            skLineSegment(sketch, "E109.3", {"start": v(43.4, -69) * mm, "end": v(43.4, -15.1) * mm});
            skLineSegment(sketch, "E109.4", {"start": v(44.6, -15.1) * mm, "end": v(43.4, -15.1) * mm});
            skLineSegment(sketch, "E109.5", {"start": v(44.6, 15.1) * mm, "end": v(44.6, -15.1) * mm});
            skLineSegment(sketch, "E109.6", {"start": v(43.4, 15.1) * mm, "end": v(44.6, 15.1) * mm});
            skLineSegment(sketch, "E109.7", {"start": v(12.6, 69.9) * mm, "end": v(12.6, 71.1) * mm});
            skLineSegment(sketch, "E109.8", {"start": v(42.5, 69.9) * mm, "end": v(12.6, 69.9) * mm});
            skArc(sketch, "E109.9", {"start": v(43.4, 69) * mm, "mid": v(43.14, 69.64) * mm, "end": v(42.5, 69.9) * mm});
            skLineSegment(sketch, "E109.10", {"start": v(43.4, 15.1) * mm, "end": v(43.4, 69) * mm});
            skLineSegment(sketch, "E109.11", {"start": v(12.6, -69.9) * mm, "end": v(12.6, -71.1) * mm});
            skLineSegment(sketch, "E109.12", {"start": v(-12.6, 71.1) * mm, "end": v(12.6, 71.1) * mm});
            skLineSegment(sketch, "E109.13", {"start": v(-12.6, -71.1) * mm, "end": v(12.6, -71.1) * mm});
            skLineSegment(sketch, "E109.14", {"start": v(-12.6, -69.9) * mm, "end": v(-12.6, -71.1) * mm});
            skLineSegment(sketch, "E109.15", {"start": v(-42.5, -69.9) * mm, "end": v(-12.6, -69.9) * mm});
            skArc(sketch, "E109.16", {"start": v(-43.4, -69) * mm, "mid": v(-43.14, -69.64) * mm, "end": v(-42.5, -69.9) * mm});
            skLineSegment(sketch, "E109.17", {"start": v(-43.4, -15.1) * mm, "end": v(-43.4, -69) * mm});
            skLineSegment(sketch, "E109.18", {"start": v(-44.6, -15.1) * mm, "end": v(-43.4, -15.1) * mm});
            skLineSegment(sketch, "E109.19", {"start": v(-44.6, 15.1) * mm, "end": v(-44.6, -15.1) * mm});
            skLineSegment(sketch, "E109.20", {"start": v(-43.4, 15.1) * mm, "end": v(-44.6, 15.1) * mm});
            skLineSegment(sketch, "E109.21", {"start": v(-43.4, 69) * mm, "end": v(-43.4, 15.1) * mm});
            skArc(sketch, "E109.22", {"start": v(-42.5, 69.9) * mm, "mid": v(-43.14, 69.64) * mm, "end": v(-43.4, 69) * mm});
            skLineSegment(sketch, "E109.23", {"start": v(-12.6, 69.9) * mm, "end": v(-42.5, 69.9) * mm});
            skSolve(sketch);
        }
        {
            var Q0;
            Q0 = qSketchRegion(id + "F18", true);
            var Q1;
            Q1=sQuery(id+"F3.wireOp",EDGE,"E58");
            sweep(context, id + "F20", {"profiles" : qUnion([Q0]), "path" : qUnion([Q1])});
        }
        {
            var Q0;
            Q0 = qSketchRegion(id + "F19", true);
            var Q1;
            Q1=sQuery(id+"F3.wireOp",EDGE,"E58");
            sweep(context, id + "F21", {"operationType" : NewBodyOperationType.REMOVE, "profiles" : qUnion([Q0]), "path" : qUnion([Q1])});
        }
        {
            var Q0;
            Q0=makeQuery(id+"F21.boolean.opBoolean","COPY",EDGE,{"derivedFrom":makeQuery(id+"F21.opSweep","SWEPT_EDGE",EDGE,{"disambiguationData":[OSD([sQuery(id+"F3.wireOp",EDGE,"E58"),sQuery(id+"F19.wireOp",EDGE,"E109.0"),sQuery(id+"F19.wireOp",EDGE,"E109.23")])]})});
            var Q1;
            Q1=makeQuery(id+"F21.boolean.opBoolean","COPY",EDGE,{"derivedFrom":makeQuery(id+"F21.opSweep","SWEPT_EDGE",EDGE,{"disambiguationData":[OSD([sQuery(id+"F3.wireOp",EDGE,"E58"),sQuery(id+"F19.wireOp",EDGE,"E109.7"),sQuery(id+"F19.wireOp",EDGE,"E109.8")])]})});
            var Q2;
            Q2=makeQuery(id+"F21.boolean.opBoolean","COPY",EDGE,{"derivedFrom":makeQuery(id+"F21.opSweep","SWEPT_EDGE",EDGE,{"disambiguationData":[OSD([sQuery(id+"F3.wireOp",EDGE,"E58"),sQuery(id+"F19.wireOp",EDGE,"E109.20"),sQuery(id+"F19.wireOp",EDGE,"E109.21")])]})});
            var Q3;
            Q3=makeQuery(id+"F21.boolean.opBoolean","COPY",EDGE,{"derivedFrom":makeQuery(id+"F21.opSweep","SWEPT_EDGE",EDGE,{"disambiguationData":[OSD([sQuery(id+"F3.wireOp",EDGE,"E58"),sQuery(id+"F19.wireOp",EDGE,"E109.17"),sQuery(id+"F19.wireOp",EDGE,"E109.18")])]})});
            var Q4;
            Q4=makeQuery(id+"F21.boolean.opBoolean","COPY",EDGE,{"derivedFrom":makeQuery(id+"F21.opSweep","SWEPT_EDGE",EDGE,{"disambiguationData":[OSD([sQuery(id+"F3.wireOp",EDGE,"E58"),sQuery(id+"F19.wireOp",EDGE,"E109.6"),sQuery(id+"F19.wireOp",EDGE,"E109.10")])]})});
            var Q5;
            Q5=makeQuery(id+"F21.boolean.opBoolean","COPY",EDGE,{"derivedFrom":makeQuery(id+"F21.opSweep","SWEPT_EDGE",EDGE,{"disambiguationData":[OSD([sQuery(id+"F3.wireOp",EDGE,"E58"),sQuery(id+"F19.wireOp",EDGE,"E109.3"),sQuery(id+"F19.wireOp",EDGE,"E109.4")])]})});
            var Q6;
            Q6=makeQuery(id+"F21.boolean.opBoolean","COPY",EDGE,{"derivedFrom":makeQuery(id+"F21.opSweep","SWEPT_EDGE",EDGE,{"disambiguationData":[OSD([sQuery(id+"F3.wireOp",EDGE,"E58"),sQuery(id+"F19.wireOp",EDGE,"E109.14"),sQuery(id+"F19.wireOp",EDGE,"E109.15")])]})});
            var Q7;
            Q7=makeQuery(id+"F21.boolean.opBoolean","COPY",EDGE,{"derivedFrom":makeQuery(id+"F21.opSweep","SWEPT_EDGE",EDGE,{"disambiguationData":[OSD([sQuery(id+"F3.wireOp",EDGE,"E58"),sQuery(id+"F19.wireOp",EDGE,"E109.1"),sQuery(id+"F19.wireOp",EDGE,"E109.11")])]})});
            fillet(context, id + "F22", {"entities" : qUnion([Q0, Q1, Q2, Q3, Q4, Q5, Q6, Q7]), "radius" : .2 * mm, "allowEdgeOverflow" : false});
        }
        {
            var Q0;
            Q0=qCreatedBy(makeId("Top.planeOp"),FACE);
            var sketch = newSketch(context, id + "F23", { "sketchPlane" : qUnion([Q0])});
            skCircle(sketch, "E110", {"center": v(0, 0) * mm, "radius": 4 * mm});
            skSolve(sketch);
        }
        {
            var Q0;
            Q0=makeQuery(id+"F23.imprint","IMPRINT",FACE,{"disambiguationData":[TD([[makeQuery(id+"F23.imprint","IMPRINT",EDGE,{"derivedFrom":sQuery(id+"F23.wireOp",EDGE,"E110")}),1.0]])]});
            extrude(context, id + "F24", {"entities" : qUnion([Q0]), "operationType" : NewBodyOperationType.REMOVE, "endBound" : BoundingType.THROUGH_ALL, "oppositeDirection" : true, "depth" : 25 * mm});
        }
        {
            var Q0;
            Q0=makeQuery(id+"F6.opSweep","CAP_FACE",FACE,{"disambiguationData":[OSD([sQuery(id+"F3.wireOp",VERTEX,"E56.end"),sQuery(id+"F4.wireOp",EDGE,"E61.bottom"),sQuery(id+"F4.wireOp",EDGE,"E61.top"),sQuery(id+"F4.wireOp",EDGE,"E61.left"),sQuery(id+"F4.wireOp",EDGE,"E61.right")])],"isStart":false});
            var Q1;
            Q1=makeQuery(id+"F20.opSweep","CAP_FACE",FACE,{"disambiguationData":[OSD([sQuery(id+"F3.wireOp",VERTEX,"E58.start"),sQuery(id+"F18.wireOp",EDGE,"E86.0"),sQuery(id+"F18.wireOp",EDGE,"E86.1"),sQuery(id+"F18.wireOp",EDGE,"E86.2"),sQuery(id+"F18.wireOp",EDGE,"E86.3"),sQuery(id+"F18.wireOp",EDGE,"E86.4"),sQuery(id+"F18.wireOp",EDGE,"E86.5"),sQuery(id+"F18.wireOp",EDGE,"E86.6"),sQuery(id+"F18.wireOp",EDGE,"E86.7"),sQuery(id+"F18.wireOp",EDGE,"E89"),sQuery(id+"F18.wireOp",EDGE,"E90.MirrorCS"),sQuery(id+"F18.wireOp",EDGE,"E91.MirrorCS"),sQuery(id+"F18.wireOp",EDGE,"E92.MirrorCS"),sQuery(id+"F18.wireOp",EDGE,"E93"),sQuery(id+"F18.wireOp",EDGE,"E94"),sQuery(id+"F18.wireOp",EDGE,"E95"),sQuery(id+"F18.wireOp",EDGE,"E96.MirrorCS"),sQuery(id+"F18.wireOp",EDGE,"E97.MirrorCS"),sQuery(id+"F18.wireOp",EDGE,"E98.MirrorCS"),sQuery(id+"F18.wireOp",EDGE,"E99"),sQuery(id+"F18.wireOp",EDGE,"E100"),sQuery(id+"F18.wireOp",EDGE,"E102"),sQuery(id+"F18.wireOp",EDGE,"E103"),sQuery(id+"F18.wireOp",EDGE,"E105"),sQuery(id+"F18.wireOp",EDGE,"E107")])],"isStart":false});
            chamfer(context, id + "F25", {"entities" : qUnion([Q0, Q1]), "width" : .2 * mm});
        }
    });
